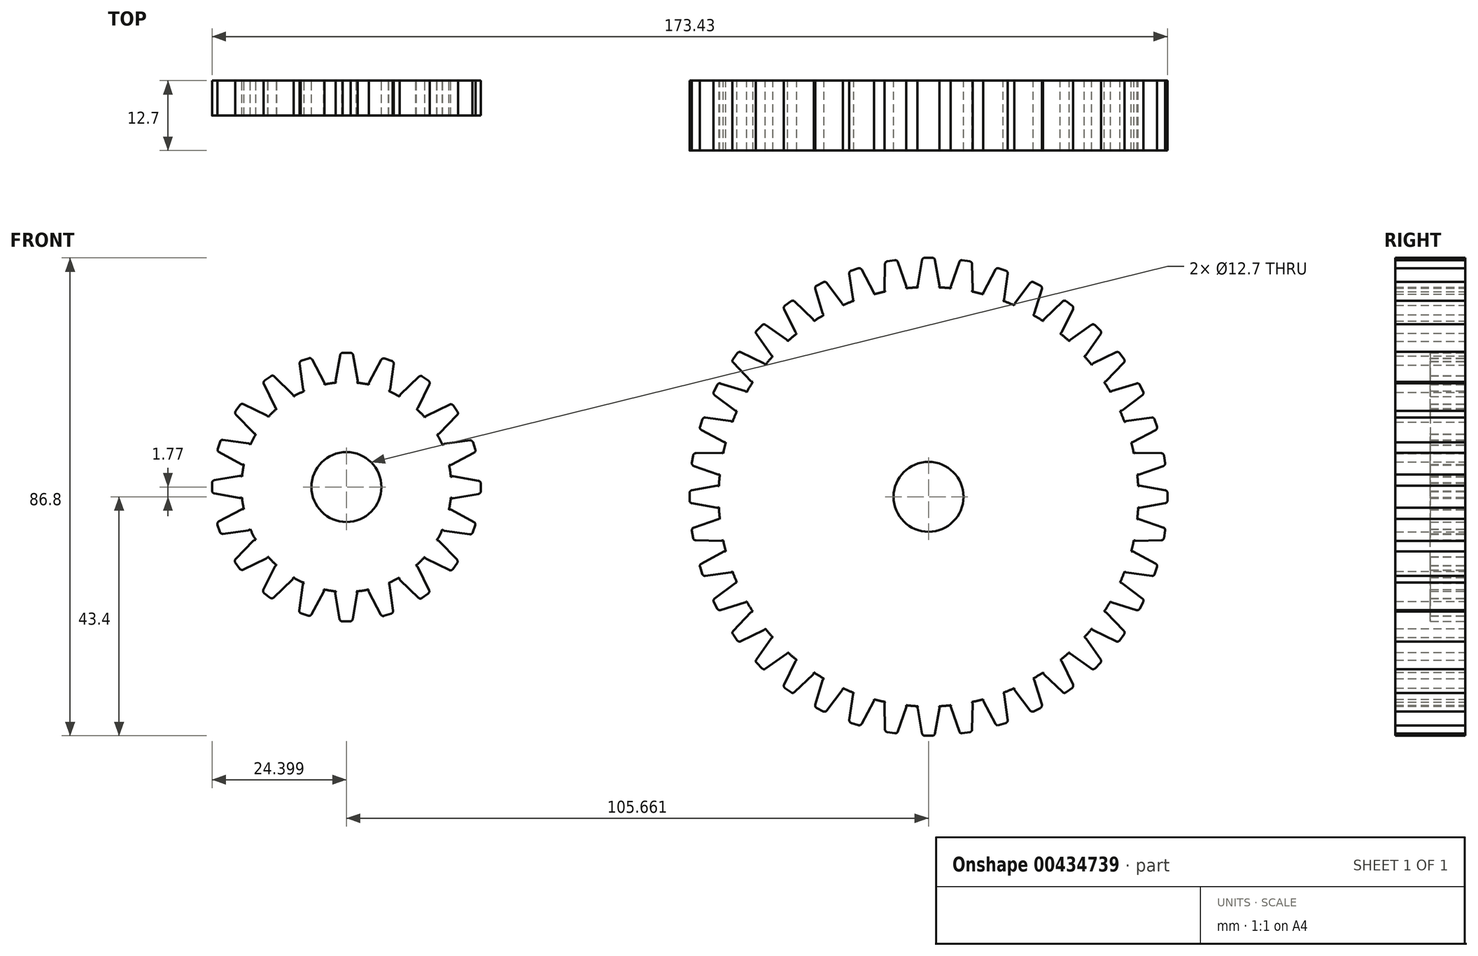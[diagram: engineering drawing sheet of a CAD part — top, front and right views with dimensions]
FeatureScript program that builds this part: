
annotation { "Feature Type Name" : "Feature", "Feature Type Description" : "" }
export const myFeature = defineFeature(function(context is Context, id is Id, definition is map)
    precondition{}
    {
        {
            var Q0;
            Q0=qCreatedBy(makeId("Front.planeOp"),FACE);
            var sketch = newSketch(context, id + "F0", { "sketchPlane" : qUnion([Q0])});
            skCircle(sketch, "E0", {"center": v(0, 0) * mm, "radius": 38.1 * mm});
            skCircle(sketch, "E1", {"center": v(-105.66, 1.77) * mm, "radius": 19.05 * mm});
            skCircle(sketch, "E2", {"center": v(0, 0) * mm, "radius": 6.35 * mm});
            skCircle(sketch, "E3", {"center": v(-105.66, 1.77) * mm, "radius": 6.35 * mm});
            skSolve(sketch);
        }
        {
            var Q0;
            Q0=makeQuery(id+"F0.imprint","IMPRINT",FACE,{"disambiguationData":[TD([[makeQuery(id+"F0.imprint","IMPRINT",EDGE,{"derivedFrom":sQuery(id+"F0.wireOp",EDGE,"E0")}),1.0]])]});
            extrude(context, id + "F1", {"entities" : qUnion([Q0]), "depth" : 12.7 * mm});
        }
        {
            var Q0;
            Q0 = qSketchRegion(id + "F0", true);
            extrude(context, id + "F2", {"entities" : qUnion([Q0]), "operationType" : NewBodyOperationType.ADD, "depth" : 6.35 * mm});
        }
        {
            var Q0;
            Q0=qCreatedBy(makeId("Front.planeOp"),FACE);
            var sketch = newSketch(context, id + "F3", { "sketchPlane" : qUnion([Q0])});
            skLineSegment(sketch, "E4", {"start": v(-1.99, 38.41) * mm, "end": v(-1.18, 42.98) * mm});
            skLineSegment(sketch, "E5", {"start": v(-0.68, 43.4) * mm, "end": v(0.68, 43.4) * mm});
            skLineSegment(sketch, "E6", {"start": v(1.18, 42.98) * mm, "end": v(1.99, 38.41) * mm});
            skLineSegment(sketch, "E7", {"start": v(-1.49, 37.82) * mm, "end": v(1.49, 37.82) * mm});
            skPoint(sketch, "E8.visualSharp", {"position": v(-1.1, 43.4) * mm});
            skArc(sketch, "E8.filletArc", {"start": v(-0.68, 43.4) * mm, "mid": v(-1, 43.29) * mm, "end": v(-1.18, 42.98) * mm});
            skPoint(sketch, "E9.visualSharp", {"position": v(1.1, 43.4) * mm});
            skArc(sketch, "E9.filletArc", {"start": v(1.18, 42.98) * mm, "mid": v(1, 43.29) * mm, "end": v(0.68, 43.4) * mm});
            skPoint(sketch, "E10.visualSharp", {"position": v(-2.1, 37.82) * mm});
            skArc(sketch, "E10.filletArc", {"start": v(-1.99, 38.41) * mm, "mid": v(-1.87, 38) * mm, "end": v(-1.49, 37.82) * mm});
            skPoint(sketch, "E11.visualSharp", {"position": v(2.1, 37.82) * mm});
            skArc(sketch, "E11.filletArc", {"start": v(1.49, 37.82) * mm, "mid": v(1.87, 38) * mm, "end": v(1.99, 38.41) * mm});
            skLineSegment(sketch, "E12", {"start": v(0, 43.4) * mm, "end": v(0, 37.82) * mm});
            skLineSegment(sketch, "E13", {"start": v(4.07, 38.25) * mm, "end": v(5.58, 42.64) * mm});
            skLineSegment(sketch, "E14", {"start": v(6.14, 42.97) * mm, "end": v(7.48, 42.76) * mm});
            skLineSegment(sketch, "E15", {"start": v(7.91, 42.27) * mm, "end": v(8, 37.63) * mm});
            skLineSegment(sketch, "E16", {"start": v(4.47, 37.58) * mm, "end": v(7.4, 37.12) * mm});
            skPoint(sketch, "E17.visualSharp", {"position": v(5.72, 43.04) * mm});
            skArc(sketch, "E17.filletArc", {"start": v(6.14, 42.97) * mm, "mid": v(5.8, 42.9) * mm, "end": v(5.58, 42.64) * mm});
            skPoint(sketch, "E18.visualSharp", {"position": v(7.9, 42.7) * mm});
            skArc(sketch, "E18.filletArc", {"start": v(7.91, 42.27) * mm, "mid": v(7.79, 42.6) * mm, "end": v(7.48, 42.76) * mm});
            skPoint(sketch, "E19.visualSharp", {"position": v(3.87, 37.68) * mm});
            skArc(sketch, "E19.filletArc", {"start": v(4.07, 38.25) * mm, "mid": v(4.11, 37.82) * mm, "end": v(4.47, 37.58) * mm});
            skPoint(sketch, "E20.visualSharp", {"position": v(8, 37.02) * mm});
            skArc(sketch, "E20.filletArc", {"start": v(7.4, 37.12) * mm, "mid": v(7.82, 37.23) * mm, "end": v(8, 37.63) * mm});
            skLineSegment(sketch, "E21", {"start": v(6.81, 42.87) * mm, "end": v(5.94, 37.35) * mm});
            skLineSegment(sketch, "E22.0", {"start": v(4.47, 37.58) * mm, "end": v(5.94, 37.35) * mm, "construction": true});
            skLineSegment(sketch, "E23.0", {"start": v(3.87, 37.68) * mm, "end": v(8, 37.02) * mm, "construction": true});
            skLineSegment(sketch, "E24", {"start": v(9.96, 37.15) * mm, "end": v(12.13, 41.25) * mm});
            skLineSegment(sketch, "E25", {"start": v(12.74, 41.5) * mm, "end": v(14.03, 41.07) * mm});
            skLineSegment(sketch, "E26", {"start": v(14.38, 40.52) * mm, "end": v(13.73, 35.92) * mm});
            skLineSegment(sketch, "E27", {"start": v(10.25, 36.43) * mm, "end": v(13.07, 35.51) * mm});
            skPoint(sketch, "E28.visualSharp", {"position": v(12.34, 41.63) * mm});
            skArc(sketch, "E28.filletArc", {"start": v(12.74, 41.5) * mm, "mid": v(12.4, 41.48) * mm, "end": v(12.13, 41.25) * mm});
            skPoint(sketch, "E29.visualSharp", {"position": v(14.44, 40.94) * mm});
            skArc(sketch, "E29.filletArc", {"start": v(14.38, 40.52) * mm, "mid": v(14.3, 40.86) * mm, "end": v(14.03, 41.07) * mm});
            skPoint(sketch, "E30.visualSharp", {"position": v(9.67, 36.62) * mm});
            skArc(sketch, "E30.filletArc", {"start": v(9.96, 37.15) * mm, "mid": v(9.93, 36.72) * mm, "end": v(10.25, 36.43) * mm});
            skPoint(sketch, "E31.visualSharp", {"position": v(13.65, 35.32) * mm});
            skArc(sketch, "E31.filletArc", {"start": v(13.07, 35.51) * mm, "mid": v(13.5, 35.56) * mm, "end": v(13.73, 35.92) * mm});
            skLineSegment(sketch, "E32", {"start": v(13.39, 41.28) * mm, "end": v(11.66, 35.97) * mm});
            skLineSegment(sketch, "E33", {"start": v(15.66, 35.12) * mm, "end": v(18.46, 38.83) * mm});
            skLineSegment(sketch, "E34", {"start": v(19.1, 38.98) * mm, "end": v(20.3, 38.36) * mm});
            skLineSegment(sketch, "E35", {"start": v(20.56, 37.76) * mm, "end": v(19.2, 33.32) * mm});
            skLineSegment(sketch, "E36", {"start": v(15.84, 34.36) * mm, "end": v(18.49, 33.02) * mm});
            skPoint(sketch, "E37.visualSharp", {"position": v(18.71, 39.17) * mm});
            skArc(sketch, "E37.filletArc", {"start": v(19.1, 38.98) * mm, "mid": v(18.75, 39.02) * mm, "end": v(18.46, 38.83) * mm});
            skPoint(sketch, "E38.visualSharp", {"position": v(20.68, 38.17) * mm});
            skArc(sketch, "E38.filletArc", {"start": v(20.56, 37.76) * mm, "mid": v(20.54, 38.1) * mm, "end": v(20.3, 38.36) * mm});
            skPoint(sketch, "E39.visualSharp", {"position": v(15.3, 34.64) * mm});
            skArc(sketch, "E39.filletArc", {"start": v(15.66, 35.12) * mm, "mid": v(15.57, 34.7) * mm, "end": v(15.84, 34.36) * mm});
            skPoint(sketch, "E40.visualSharp", {"position": v(19.02, 32.74) * mm});
            skArc(sketch, "E40.filletArc", {"start": v(18.49, 33.02) * mm, "mid": v(18.91, 33) * mm, "end": v(19.2, 33.32) * mm});
            skLineSegment(sketch, "E41", {"start": v(19.7, 38.67) * mm, "end": v(17.16, 33.7) * mm});
            skLineSegment(sketch, "E42.0", {"start": v(15.84, 34.36) * mm, "end": v(17.16, 33.7) * mm, "construction": true});
            skLineSegment(sketch, "E43.0", {"start": v(15.3, 34.64) * mm, "end": v(19.02, 32.74) * mm, "construction": true});
            skLineSegment(sketch, "E44.0", {"start": v(10.25, 36.43) * mm, "end": v(11.66, 35.97) * mm, "construction": true});
            skLineSegment(sketch, "E45.0", {"start": v(9.67, 36.62) * mm, "end": v(13.65, 35.32) * mm, "construction": true});
            skLineSegment(sketch, "E46", {"start": v(20.97, 32.26) * mm, "end": v(24.3, 35.48) * mm});
            skLineSegment(sketch, "E47", {"start": v(24.96, 35.53) * mm, "end": v(26.06, 34.73) * mm});
            skLineSegment(sketch, "E48", {"start": v(26.22, 34.1) * mm, "end": v(24.18, 29.92) * mm});
            skLineSegment(sketch, "E49", {"start": v(21.02, 31.48) * mm, "end": v(23.43, 29.73) * mm});
            skPoint(sketch, "E50.visualSharp", {"position": v(24.61, 35.78) * mm});
            skArc(sketch, "E50.filletArc", {"start": v(24.96, 35.53) * mm, "mid": v(24.62, 35.62) * mm, "end": v(24.3, 35.48) * mm});
            skPoint(sketch, "E51.visualSharp", {"position": v(26.4, 34.48) * mm});
            skArc(sketch, "E51.filletArc", {"start": v(26.22, 34.1) * mm, "mid": v(26.25, 34.44) * mm, "end": v(26.06, 34.73) * mm});
            skPoint(sketch, "E52.visualSharp", {"position": v(20.53, 31.84) * mm});
            skArc(sketch, "E52.filletArc", {"start": v(20.97, 32.26) * mm, "mid": v(20.81, 31.85) * mm, "end": v(21.02, 31.48) * mm});
            skPoint(sketch, "E53.visualSharp", {"position": v(23.91, 29.38) * mm});
            skArc(sketch, "E53.filletArc", {"start": v(23.43, 29.73) * mm, "mid": v(23.85, 29.65) * mm, "end": v(24.18, 29.92) * mm});
            skLineSegment(sketch, "E54", {"start": v(25.5, 35.13) * mm, "end": v(22.22, 30.6) * mm});
            skLineSegment(sketch, "E55", {"start": v(25.77, 28.56) * mm, "end": v(29.57, 31.23) * mm});
            skLineSegment(sketch, "E56", {"start": v(30.22, 31.17) * mm, "end": v(31.18, 30.2) * mm});
            skLineSegment(sketch, "E57", {"start": v(31.24, 29.56) * mm, "end": v(28.58, 25.75) * mm});
            skLineSegment(sketch, "E58", {"start": v(25.7, 27.79) * mm, "end": v(27.8, 25.69) * mm});
            skPoint(sketch, "E59.visualSharp", {"position": v(29.92, 31.47) * mm});
            skArc(sketch, "E59.filletArc", {"start": v(30.22, 31.17) * mm, "mid": v(29.9, 31.32) * mm, "end": v(29.57, 31.23) * mm});
            skPoint(sketch, "E60.visualSharp", {"position": v(31.48, 29.9) * mm});
            skArc(sketch, "E60.filletArc", {"start": v(31.24, 29.56) * mm, "mid": v(31.33, 29.9) * mm, "end": v(31.18, 30.2) * mm});
            skPoint(sketch, "E61.visualSharp", {"position": v(25.27, 28.22) * mm});
            skArc(sketch, "E61.filletArc", {"start": v(25.77, 28.56) * mm, "mid": v(25.55, 28.2) * mm, "end": v(25.7, 27.79) * mm});
            skPoint(sketch, "E62.visualSharp", {"position": v(28.23, 25.26) * mm});
            skArc(sketch, "E62.filletArc", {"start": v(27.8, 25.69) * mm, "mid": v(28.2, 25.54) * mm, "end": v(28.58, 25.75) * mm});
            skLineSegment(sketch, "E63", {"start": v(30.7, 30.69) * mm, "end": v(26.75, 26.74) * mm});
            skLineSegment(sketch, "E64.0", {"start": v(25.7, 27.79) * mm, "end": v(26.75, 26.74) * mm, "construction": true});
            skLineSegment(sketch, "E65.0", {"start": v(25.27, 28.22) * mm, "end": v(28.23, 25.26) * mm, "construction": true});
            skLineSegment(sketch, "E66", {"start": v(29.89, 24.22) * mm, "end": v(34.06, 26.25) * mm});
            skLineSegment(sketch, "E67", {"start": v(34.7, 26.1) * mm, "end": v(35.5, 25) * mm});
            skLineSegment(sketch, "E68", {"start": v(35.45, 24.34) * mm, "end": v(32.22, 21) * mm});
            skLineSegment(sketch, "E69", {"start": v(29.7, 23.46) * mm, "end": v(31.44, 21.06) * mm});
            skPoint(sketch, "E70.visualSharp", {"position": v(34.44, 26.44) * mm});
            skArc(sketch, "E70.filletArc", {"start": v(34.7, 26.1) * mm, "mid": v(34.4, 26.29) * mm, "end": v(34.06, 26.25) * mm});
            skPoint(sketch, "E71.visualSharp", {"position": v(35.74, 24.65) * mm});
            skArc(sketch, "E71.filletArc", {"start": v(35.45, 24.34) * mm, "mid": v(35.59, 24.66) * mm, "end": v(35.5, 25) * mm});
            skPoint(sketch, "E72.visualSharp", {"position": v(29.34, 23.95) * mm});
            skArc(sketch, "E72.filletArc", {"start": v(29.89, 24.22) * mm, "mid": v(29.62, 23.88) * mm, "end": v(29.7, 23.46) * mm});
            skPoint(sketch, "E73.visualSharp", {"position": v(31.8, 20.57) * mm});
            skArc(sketch, "E73.filletArc", {"start": v(31.44, 21.06) * mm, "mid": v(31.82, 20.85) * mm, "end": v(32.22, 21) * mm});
            skLineSegment(sketch, "E74", {"start": v(35.1, 25.54) * mm, "end": v(30.57, 22.26) * mm});
            skLineSegment(sketch, "E75", {"start": v(33.31, 19.22) * mm, "end": v(37.75, 20.58) * mm});
            skLineSegment(sketch, "E76", {"start": v(38.35, 20.32) * mm, "end": v(38.97, 19.11) * mm});
            skLineSegment(sketch, "E77", {"start": v(38.82, 18.47) * mm, "end": v(35.11, 15.68) * mm});
            skLineSegment(sketch, "E78", {"start": v(33, 18.5) * mm, "end": v(34.36, 15.86) * mm});
            skPoint(sketch, "E79.visualSharp", {"position": v(38.16, 20.7) * mm});
            skArc(sketch, "E79.filletArc", {"start": v(38.35, 20.32) * mm, "mid": v(38.1, 20.56) * mm, "end": v(37.75, 20.58) * mm});
            skPoint(sketch, "E80.visualSharp", {"position": v(39.16, 18.73) * mm});
            skArc(sketch, "E80.filletArc", {"start": v(38.82, 18.47) * mm, "mid": v(39.01, 18.77) * mm, "end": v(38.97, 19.11) * mm});
            skPoint(sketch, "E81.visualSharp", {"position": v(32.73, 19.04) * mm});
            skArc(sketch, "E81.filletArc", {"start": v(33.31, 19.22) * mm, "mid": v(33, 18.93) * mm, "end": v(33, 18.5) * mm});
            skPoint(sketch, "E82.visualSharp", {"position": v(34.63, 15.32) * mm});
            skArc(sketch, "E82.filletArc", {"start": v(34.36, 15.86) * mm, "mid": v(34.7, 15.6) * mm, "end": v(35.11, 15.68) * mm});
            skLineSegment(sketch, "E83", {"start": v(38.66, 19.72) * mm, "end": v(33.68, 17.18) * mm});
            skLineSegment(sketch, "E84.0", {"start": v(33, 18.5) * mm, "end": v(33.68, 17.18) * mm, "construction": true});
            skLineSegment(sketch, "E85.0", {"start": v(32.73, 19.04) * mm, "end": v(34.63, 15.32) * mm, "construction": true});
            skLineSegment(sketch, "E86.0", {"start": v(29.7, 23.46) * mm, "end": v(30.57, 22.26) * mm, "construction": true});
            skLineSegment(sketch, "E87.0", {"start": v(29.34, 23.95) * mm, "end": v(31.8, 20.57) * mm, "construction": true});
            skLineSegment(sketch, "E88.0", {"start": v(21.02, 31.48) * mm, "end": v(22.22, 30.6) * mm, "construction": true});
            skLineSegment(sketch, "E89.0", {"start": v(20.53, 31.84) * mm, "end": v(23.91, 29.38) * mm, "construction": true});
            skLineSegment(sketch, "E90", {"start": v(35.9, 13.73) * mm, "end": v(40.5, 14.38) * mm});
            skLineSegment(sketch, "E91", {"start": v(41.05, 14.03) * mm, "end": v(41.47, 12.74) * mm});
            skLineSegment(sketch, "E92", {"start": v(41.23, 12.14) * mm, "end": v(37.13, 9.96) * mm});
            skLineSegment(sketch, "E93", {"start": v(35.5, 13.07) * mm, "end": v(36.4, 10.25) * mm});
            skPoint(sketch, "E94.visualSharp", {"position": v(40.92, 14.44) * mm});
            skArc(sketch, "E94.filletArc", {"start": v(41.05, 14.03) * mm, "mid": v(40.84, 14.3) * mm, "end": v(40.5, 14.38) * mm});
            skPoint(sketch, "E95.visualSharp", {"position": v(41.6, 12.34) * mm});
            skArc(sketch, "E95.filletArc", {"start": v(41.23, 12.14) * mm, "mid": v(41.46, 12.4) * mm, "end": v(41.47, 12.74) * mm});
            skPoint(sketch, "E96.visualSharp", {"position": v(35.3, 13.65) * mm});
            skArc(sketch, "E96.filletArc", {"start": v(35.9, 13.73) * mm, "mid": v(35.54, 13.5) * mm, "end": v(35.5, 13.07) * mm});
            skPoint(sketch, "E97.visualSharp", {"position": v(36.6, 9.67) * mm});
            skArc(sketch, "E97.filletArc", {"start": v(36.4, 10.25) * mm, "mid": v(36.7, 9.93) * mm, "end": v(37.13, 9.96) * mm});
            skLineSegment(sketch, "E98", {"start": v(41.26, 13.39) * mm, "end": v(35.95, 11.66) * mm});
            skLineSegment(sketch, "E99.0", {"start": v(35.5, 13.07) * mm, "end": v(35.95, 11.66) * mm, "construction": true});
            skLineSegment(sketch, "E100", {"start": v(37.6, 8) * mm, "end": v(42.24, 7.9) * mm});
            skLineSegment(sketch, "E101", {"start": v(42.73, 7.48) * mm, "end": v(42.95, 6.14) * mm});
            skLineSegment(sketch, "E102", {"start": v(42.6, 5.58) * mm, "end": v(38.22, 4.07) * mm});
            skLineSegment(sketch, "E103", {"start": v(37.09, 7.4) * mm, "end": v(37.55, 4.47) * mm});
            skPoint(sketch, "E104.visualSharp", {"position": v(42.67, 7.9) * mm});
            skArc(sketch, "E104.filletArc", {"start": v(42.73, 7.48) * mm, "mid": v(42.56, 7.79) * mm, "end": v(42.24, 7.9) * mm});
            skPoint(sketch, "E105.visualSharp", {"position": v(43.01, 5.72) * mm});
            skArc(sketch, "E105.filletArc", {"start": v(42.6, 5.58) * mm, "mid": v(42.88, 5.8) * mm, "end": v(42.95, 6.14) * mm});
            skPoint(sketch, "E106.visualSharp", {"position": v(37, 8) * mm});
            skArc(sketch, "E106.filletArc", {"start": v(37.6, 8) * mm, "mid": v(37.2, 7.82) * mm, "end": v(37.09, 7.4) * mm});
            skPoint(sketch, "E107.visualSharp", {"position": v(37.65, 3.87) * mm});
            skArc(sketch, "E107.filletArc", {"start": v(37.55, 4.47) * mm, "mid": v(37.8, 4.11) * mm, "end": v(38.22, 4.07) * mm});
            skLineSegment(sketch, "E108", {"start": v(42.84, 6.81) * mm, "end": v(37.32, 5.94) * mm});
            skLineSegment(sketch, "E109", {"start": v(38.38, 1.99) * mm, "end": v(42.95, 1.18) * mm});
            skLineSegment(sketch, "E110", {"start": v(43.37, 0.68) * mm, "end": v(43.37, -0.68) * mm});
            skLineSegment(sketch, "E111", {"start": v(42.95, -1.18) * mm, "end": v(38.38, -1.99) * mm});
            skLineSegment(sketch, "E112", {"start": v(37.79, 1.48) * mm, "end": v(37.79, -1.49) * mm});
            skPoint(sketch, "E113.visualSharp", {"position": v(43.37, 1.1) * mm});
            skArc(sketch, "E113.filletArc", {"start": v(43.37, 0.68) * mm, "mid": v(43.25, 1) * mm, "end": v(42.95, 1.18) * mm});
            skPoint(sketch, "E114.visualSharp", {"position": v(43.37, -1.1) * mm});
            skArc(sketch, "E114.filletArc", {"start": v(42.95, -1.18) * mm, "mid": v(43.25, -1) * mm, "end": v(43.37, -0.68) * mm});
            skPoint(sketch, "E115.visualSharp", {"position": v(37.79, 2.1) * mm});
            skArc(sketch, "E115.filletArc", {"start": v(38.38, 1.99) * mm, "mid": v(37.97, 1.87) * mm, "end": v(37.79, 1.48) * mm});
            skPoint(sketch, "E116.visualSharp", {"position": v(37.79, -2.1) * mm});
            skArc(sketch, "E116.filletArc", {"start": v(37.79, -1.49) * mm, "mid": v(37.97, -1.88) * mm, "end": v(38.38, -1.99) * mm});
            skLineSegment(sketch, "E117", {"start": v(43.37, 0) * mm, "end": v(37.79, 0) * mm});
            skLineSegment(sketch, "E118.0", {"start": v(37.79, 1.48) * mm, "end": v(37.79, 0) * mm, "construction": true});
            skLineSegment(sketch, "E119.0", {"start": v(37.79, 2.1) * mm, "end": v(37.79, -2.1) * mm, "construction": true});
            skLineSegment(sketch, "E120.0", {"start": v(37.09, 7.4) * mm, "end": v(37.32, 5.94) * mm, "construction": true});
            skLineSegment(sketch, "E121.0", {"start": v(37, 8) * mm, "end": v(37.65, 3.87) * mm, "construction": true});
            skArc(sketch, "E122.MirrorCS", {"start": v(-4.07, 38.25) * mm, "mid": v(-4.11, 37.82) * mm, "end": v(-4.47, 37.58) * mm});
            skArc(sketch, "E123.MirrorCS", {"start": v(-37.6, 8) * mm, "mid": v(-37.2, 7.82) * mm, "end": v(-37.09, 7.4) * mm});
            skLineSegment(sketch, "E124.MirrorCS", {"start": v(-37.09, 7.4) * mm, "end": v(-37.32, 5.94) * mm, "construction": true});
            skLineSegment(sketch, "E125.MirrorCS", {"start": v(-4.47, 37.58) * mm, "end": v(-5.94, 37.35) * mm, "construction": true});
            skLineSegment(sketch, "E126.MirrorCS", {"start": v(-4.47, 37.58) * mm, "end": v(-7.4, 37.12) * mm});
            skArc(sketch, "E127.MirrorCS", {"start": v(-27.8, 25.69) * mm, "mid": v(-28.2, 25.54) * mm, "end": v(-28.58, 25.75) * mm});
            skLineSegment(sketch, "E128.MirrorCS", {"start": v(-33, 18.5) * mm, "end": v(-34.36, 15.86) * mm});
            skArc(sketch, "E129.MirrorCS", {"start": v(-25.77, 28.56) * mm, "mid": v(-25.55, 28.2) * mm, "end": v(-25.7, 27.79) * mm});
            skArc(sketch, "E130.MirrorCS", {"start": v(-9.96, 37.15) * mm, "mid": v(-9.93, 36.72) * mm, "end": v(-10.25, 36.43) * mm});
            skLineSegment(sketch, "E131.MirrorCS", {"start": v(-35.5, 13.07) * mm, "end": v(-35.95, 11.66) * mm, "construction": true});
            skArc(sketch, "E132.MirrorCS", {"start": v(-38.38, 1.99) * mm, "mid": v(-37.97, 1.87) * mm, "end": v(-37.79, 1.48) * mm});
            skLineSegment(sketch, "E133.MirrorCS", {"start": v(-10.25, 36.43) * mm, "end": v(-11.66, 35.97) * mm, "construction": true});
            skLineSegment(sketch, "E134.MirrorCS", {"start": v(-25.7, 27.79) * mm, "end": v(-27.8, 25.69) * mm});
            skArc(sketch, "E135.MirrorCS", {"start": v(-29.89, 24.22) * mm, "mid": v(-29.62, 23.88) * mm, "end": v(-29.7, 23.46) * mm});
            skLineSegment(sketch, "E136.MirrorCS", {"start": v(-21.02, 31.48) * mm, "end": v(-22.22, 30.6) * mm, "construction": true});
            skLineSegment(sketch, "E137.MirrorCS", {"start": v(-37.09, 7.4) * mm, "end": v(-37.55, 4.47) * mm});
            skLineSegment(sketch, "E138.MirrorCS", {"start": v(-3.87, 37.68) * mm, "end": v(-8, 37.02) * mm, "construction": true});
            skLineSegment(sketch, "E139.MirrorCS", {"start": v(-29.7, 23.46) * mm, "end": v(-30.57, 22.26) * mm, "construction": true});
            skLineSegment(sketch, "E140.MirrorCS", {"start": v(-37.79, 1.48) * mm, "end": v(-37.79, 0) * mm, "construction": true});
            skLineSegment(sketch, "E141.MirrorCS", {"start": v(-21.02, 31.48) * mm, "end": v(-23.43, 29.73) * mm});
            skLineSegment(sketch, "E142.MirrorCS", {"start": v(-25.27, 28.22) * mm, "end": v(-28.23, 25.26) * mm, "construction": true});
            skArc(sketch, "E143.MirrorCS", {"start": v(-33.31, 19.22) * mm, "mid": v(-33, 18.93) * mm, "end": v(-33, 18.5) * mm});
            skArc(sketch, "E144.MirrorCS", {"start": v(-7.4, 37.12) * mm, "mid": v(-7.82, 37.23) * mm, "end": v(-8, 37.63) * mm});
            skLineSegment(sketch, "E145.MirrorCS", {"start": v(-33, 18.5) * mm, "end": v(-33.68, 17.18) * mm, "construction": true});
            skArc(sketch, "E146.MirrorCS", {"start": v(-35.9, 13.73) * mm, "mid": v(-35.54, 13.5) * mm, "end": v(-35.5, 13.07) * mm});
            skArc(sketch, "E147.MirrorCS", {"start": v(-20.97, 32.26) * mm, "mid": v(-20.81, 31.85) * mm, "end": v(-21.02, 31.48) * mm});
            skLineSegment(sketch, "E148.MirrorCS", {"start": v(-25.7, 27.79) * mm, "end": v(-26.75, 26.74) * mm, "construction": true});
            skLineSegment(sketch, "E149.MirrorCS", {"start": v(-15.84, 34.36) * mm, "end": v(-18.49, 33.02) * mm});
            skLineSegment(sketch, "E150.MirrorCS", {"start": v(-35.5, 13.07) * mm, "end": v(-36.4, 10.25) * mm});
            skLineSegment(sketch, "E151.MirrorCS", {"start": v(-9.67, 36.62) * mm, "end": v(-13.65, 35.32) * mm, "construction": true});
            skArc(sketch, "E152.MirrorCS", {"start": v(-37.55, 4.47) * mm, "mid": v(-37.8, 4.11) * mm, "end": v(-38.22, 4.07) * mm});
            skLineSegment(sketch, "E153.MirrorCS", {"start": v(-10.25, 36.43) * mm, "end": v(-13.07, 35.51) * mm});
            skLineSegment(sketch, "E154.MirrorCS", {"start": v(-15.3, 34.64) * mm, "end": v(-19.02, 32.74) * mm, "construction": true});
            skArc(sketch, "E155.MirrorCS", {"start": v(-1.49, 37.82) * mm, "mid": v(-1.87, 38) * mm, "end": v(-1.99, 38.41) * mm});
            skLineSegment(sketch, "E156.MirrorCS", {"start": v(1.49, 37.82) * mm, "end": v(-1.49, 37.82) * mm});
            skArc(sketch, "E157.MirrorCS", {"start": v(-26.22, 34.1) * mm, "mid": v(-26.25, 34.44) * mm, "end": v(-26.06, 34.73) * mm});
            skLineSegment(sketch, "E158.MirrorCS", {"start": v(-38.35, 20.32) * mm, "end": v(-38.97, 19.11) * mm});
            skLineSegment(sketch, "E159.MirrorCS", {"start": v(-15.84, 34.36) * mm, "end": v(-17.16, 33.7) * mm, "construction": true});
            skArc(sketch, "E160.MirrorCS", {"start": v(-31.44, 21.06) * mm, "mid": v(-31.82, 20.85) * mm, "end": v(-32.22, 21) * mm});
            skLineSegment(sketch, "E161.MirrorCS", {"start": v(-20.53, 31.84) * mm, "end": v(-23.91, 29.38) * mm, "construction": true});
            skLineSegment(sketch, "E162.MirrorCS", {"start": v(-37, 8) * mm, "end": v(-37.65, 3.87) * mm, "construction": true});
            skArc(sketch, "E163.MirrorCS", {"start": v(-18.49, 33.02) * mm, "mid": v(-18.91, 33) * mm, "end": v(-19.2, 33.32) * mm});
            skLineSegment(sketch, "E164.MirrorCS", {"start": v(-19.1, 38.98) * mm, "end": v(-20.3, 38.36) * mm});
            skArc(sketch, "E165.MirrorCS", {"start": v(-24.96, 35.53) * mm, "mid": v(-24.62, 35.62) * mm, "end": v(-24.3, 35.48) * mm});
            skArc(sketch, "E166.MirrorCS", {"start": v(-34.36, 15.86) * mm, "mid": v(-34.7, 15.6) * mm, "end": v(-35.11, 15.68) * mm});
            skLineSegment(sketch, "E167.MirrorCS", {"start": v(-24.96, 35.53) * mm, "end": v(-26.06, 34.73) * mm});
            skArc(sketch, "E168.MirrorCS", {"start": v(-13.07, 35.51) * mm, "mid": v(-13.5, 35.56) * mm, "end": v(-13.73, 35.92) * mm});
            skArc(sketch, "E169.MirrorCS", {"start": v(-15.66, 35.12) * mm, "mid": v(-15.57, 34.7) * mm, "end": v(-15.84, 34.36) * mm});
            skArc(sketch, "E170.MirrorCS", {"start": v(-20.56, 37.76) * mm, "mid": v(-20.54, 38.1) * mm, "end": v(-20.3, 38.36) * mm});
            skArc(sketch, "E171.MirrorCS", {"start": v(-23.43, 29.73) * mm, "mid": v(-23.85, 29.65) * mm, "end": v(-24.18, 29.92) * mm});
            skLineSegment(sketch, "E172.MirrorCS", {"start": v(-32.73, 19.04) * mm, "end": v(-34.63, 15.32) * mm, "construction": true});
            skArc(sketch, "E173.MirrorCS", {"start": v(-19.1, 38.98) * mm, "mid": v(-18.75, 39.02) * mm, "end": v(-18.46, 38.83) * mm});
            skArc(sketch, "E174.MirrorCS", {"start": v(-38.82, 18.47) * mm, "mid": v(-39.01, 18.77) * mm, "end": v(-38.97, 19.11) * mm});
            skArc(sketch, "E175.MirrorCS", {"start": v(-41.23, 12.14) * mm, "mid": v(-41.46, 12.4) * mm, "end": v(-41.47, 12.74) * mm});
            skLineSegment(sketch, "E176.MirrorCS", {"start": v(-37.79, 1.48) * mm, "end": v(-37.79, -1.49) * mm});
            skLineSegment(sketch, "E177.MirrorCS", {"start": v(-29.7, 23.46) * mm, "end": v(-31.44, 21.06) * mm});
            skArc(sketch, "E178.MirrorCS", {"start": v(-36.4, 10.25) * mm, "mid": v(-36.7, 9.93) * mm, "end": v(-37.13, 9.96) * mm});
            skArc(sketch, "E179.MirrorCS", {"start": v(-14.38, 40.52) * mm, "mid": v(-14.3, 40.86) * mm, "end": v(-14.03, 41.07) * mm});
            skLineSegment(sketch, "E180.MirrorCS", {"start": v(-41.05, 14.03) * mm, "end": v(-41.47, 12.74) * mm});
            skArc(sketch, "E181.MirrorCS", {"start": v(-30.22, 31.17) * mm, "mid": v(-29.9, 31.32) * mm, "end": v(-29.57, 31.23) * mm});
            skArc(sketch, "E182.MirrorCS", {"start": v(1.99, 38.41) * mm, "mid": v(1.87, 38) * mm, "end": v(1.49, 37.82) * mm});
            skArc(sketch, "E183.MirrorCS", {"start": v(-1.18, 42.98) * mm, "mid": v(-1, 43.29) * mm, "end": v(-0.68, 43.4) * mm});
            skArc(sketch, "E184.MirrorCS", {"start": v(0.68, 43.4) * mm, "mid": v(1, 43.29) * mm, "end": v(1.18, 42.98) * mm});
            skLineSegment(sketch, "E185.MirrorCS", {"start": v(0.68, 43.4) * mm, "end": v(-0.68, 43.4) * mm});
            skArc(sketch, "E186.MirrorCS", {"start": v(-41.05, 14.03) * mm, "mid": v(-40.84, 14.3) * mm, "end": v(-40.5, 14.38) * mm});
            skArc(sketch, "E187.MirrorCS", {"start": v(-38.35, 20.32) * mm, "mid": v(-38.1, 20.56) * mm, "end": v(-37.75, 20.58) * mm});
            skLineSegment(sketch, "E188.MirrorCS", {"start": v(-6.14, 42.97) * mm, "end": v(-7.48, 42.76) * mm});
            skLineSegment(sketch, "E189.MirrorCS", {"start": v(-41.23, 12.14) * mm, "end": v(-37.13, 9.96) * mm});
            skLineSegment(sketch, "E190.MirrorCS", {"start": v(-34.7, 26.1) * mm, "end": v(-35.5, 25) * mm});
            skArc(sketch, "E191.MirrorCS", {"start": v(-12.74, 41.5) * mm, "mid": v(-12.4, 41.48) * mm, "end": v(-12.13, 41.25) * mm});
            skArc(sketch, "E192.MirrorCS", {"start": v(-31.24, 29.56) * mm, "mid": v(-31.33, 29.9) * mm, "end": v(-31.18, 30.2) * mm});
            skArc(sketch, "E193.MirrorCS", {"start": v(-42.6, 5.58) * mm, "mid": v(-42.88, 5.8) * mm, "end": v(-42.95, 6.14) * mm});
            skLineSegment(sketch, "E194.MirrorCS", {"start": v(-12.74, 41.5) * mm, "end": v(-14.03, 41.07) * mm});
            skArc(sketch, "E195.MirrorCS", {"start": v(-42.73, 7.48) * mm, "mid": v(-42.56, 7.79) * mm, "end": v(-42.24, 7.9) * mm});
            skLineSegment(sketch, "E196.MirrorCS", {"start": v(-30.22, 31.17) * mm, "end": v(-31.18, 30.2) * mm});
            skArc(sketch, "E197.MirrorCS", {"start": v(-35.45, 24.34) * mm, "mid": v(-35.59, 24.66) * mm, "end": v(-35.5, 25) * mm});
            skLineSegment(sketch, "E198.MirrorCS", {"start": v(-29.34, 23.95) * mm, "end": v(-31.8, 20.57) * mm, "construction": true});
            skArc(sketch, "E199.MirrorCS", {"start": v(-7.91, 42.27) * mm, "mid": v(-7.79, 42.6) * mm, "end": v(-7.48, 42.76) * mm});
            skLineSegment(sketch, "E200.MirrorCS", {"start": v(-37.79, 2.1) * mm, "end": v(-37.79, -2.1) * mm, "construction": true});
            skArc(sketch, "E201.MirrorCS", {"start": v(-34.7, 26.1) * mm, "mid": v(-34.4, 26.29) * mm, "end": v(-34.06, 26.25) * mm});
            skArc(sketch, "E202.MirrorCS", {"start": v(-6.14, 42.97) * mm, "mid": v(-5.8, 42.9) * mm, "end": v(-5.58, 42.64) * mm});
            skArc(sketch, "E203.MirrorCS", {"start": v(-37.79, -1.49) * mm, "mid": v(-37.97, -1.88) * mm, "end": v(-38.38, -1.99) * mm});
            skLineSegment(sketch, "E204.MirrorCS", {"start": v(-42.73, 7.48) * mm, "end": v(-42.95, 6.14) * mm});
            skLineSegment(sketch, "E205.MirrorCS", {"start": v(-35.45, 24.34) * mm, "end": v(-32.22, 21) * mm});
            skLineSegment(sketch, "E206.MirrorCS", {"start": v(-20.97, 32.26) * mm, "end": v(-24.3, 35.48) * mm});
            skLineSegment(sketch, "E207.MirrorCS", {"start": v(-43.37, 0.68) * mm, "end": v(-43.37, -0.68) * mm});
            skArc(sketch, "E208.MirrorCS", {"start": v(-42.95, -1.18) * mm, "mid": v(-43.25, -1) * mm, "end": v(-43.37, -0.68) * mm});
            skLineSegment(sketch, "E209.MirrorCS", {"start": v(-9.96, 37.15) * mm, "end": v(-12.13, 41.25) * mm});
            skLineSegment(sketch, "E210.MirrorCS", {"start": v(-25.77, 28.56) * mm, "end": v(-29.57, 31.23) * mm});
            skLineSegment(sketch, "E211.MirrorCS", {"start": v(-15.66, 35.12) * mm, "end": v(-18.46, 38.83) * mm});
            skArc(sketch, "E212.MirrorCS", {"start": v(-43.37, 0.68) * mm, "mid": v(-43.25, 1) * mm, "end": v(-42.95, 1.18) * mm});
            skLineSegment(sketch, "E213.MirrorCS", {"start": v(-38.82, 18.47) * mm, "end": v(-35.11, 15.68) * mm});
            skLineSegment(sketch, "E214.MirrorCS", {"start": v(-4.07, 38.25) * mm, "end": v(-5.58, 42.64) * mm});
            skLineSegment(sketch, "E215.MirrorCS", {"start": v(-20.56, 37.76) * mm, "end": v(-19.2, 33.32) * mm});
            skLineSegment(sketch, "E216.MirrorCS", {"start": v(-19.7, 38.67) * mm, "end": v(-17.16, 33.7) * mm});
            skLineSegment(sketch, "E217.MirrorCS", {"start": v(-31.24, 29.56) * mm, "end": v(-28.58, 25.75) * mm});
            skLineSegment(sketch, "E218.MirrorCS", {"start": v(-42.6, 5.58) * mm, "end": v(-38.22, 4.07) * mm});
            skLineSegment(sketch, "E219.MirrorCS", {"start": v(-26.22, 34.1) * mm, "end": v(-24.18, 29.92) * mm});
            skPoint(sketch, "E220.MirrorP", {"position": v(-13.65, 35.32) * mm});
            skLineSegment(sketch, "E221.MirrorCS", {"start": v(-38.38, 1.99) * mm, "end": v(-42.95, 1.18) * mm});
            skLineSegment(sketch, "E222.MirrorCS", {"start": v(-33.31, 19.22) * mm, "end": v(-37.75, 20.58) * mm});
            skPoint(sketch, "E223.MirrorP", {"position": v(-31.8, 20.57) * mm});
            skPoint(sketch, "E224.MirrorP", {"position": v(-36.6, 9.67) * mm});
            skLineSegment(sketch, "E225.MirrorCS", {"start": v(-1.18, 42.98) * mm, "end": v(-1.99, 38.41) * mm});
            skLineSegment(sketch, "E226.MirrorCS", {"start": v(1.99, 38.41) * mm, "end": v(1.18, 42.98) * mm});
            skLineSegment(sketch, "E227.MirrorCS", {"start": v(-7.91, 42.27) * mm, "end": v(-8, 37.63) * mm});
            skLineSegment(sketch, "E228.MirrorCS", {"start": v(-42.84, 6.81) * mm, "end": v(-37.32, 5.94) * mm});
            skLineSegment(sketch, "E229.MirrorCS", {"start": v(-38.66, 19.72) * mm, "end": v(-33.68, 17.18) * mm});
            skPoint(sketch, "E230.MirrorP", {"position": v(-37.65, 3.87) * mm});
            skPoint(sketch, "E231.MirrorP", {"position": v(-8, 37.02) * mm});
            skPoint(sketch, "E232.MirrorP", {"position": v(-28.23, 25.26) * mm});
            skPoint(sketch, "E233.MirrorP", {"position": v(-34.63, 15.32) * mm});
            skLineSegment(sketch, "E234.MirrorCS", {"start": v(-35.1, 25.54) * mm, "end": v(-30.57, 22.26) * mm});
            skLineSegment(sketch, "E235.MirrorCS", {"start": v(-35.9, 13.73) * mm, "end": v(-40.5, 14.38) * mm});
            skLineSegment(sketch, "E236.MirrorCS", {"start": v(-14.38, 40.52) * mm, "end": v(-13.73, 35.92) * mm});
            skPoint(sketch, "E237.MirrorP", {"position": v(-35.3, 13.65) * mm});
            skPoint(sketch, "E238.MirrorP", {"position": v(-37.79, 2.1) * mm});
            skLineSegment(sketch, "E239.MirrorCS", {"start": v(-41.26, 13.39) * mm, "end": v(-35.95, 11.66) * mm});
            skLineSegment(sketch, "E240.MirrorCS", {"start": v(-29.89, 24.22) * mm, "end": v(-34.06, 26.25) * mm});
            skLineSegment(sketch, "E241.MirrorCS", {"start": v(-30.7, 30.69) * mm, "end": v(-26.75, 26.74) * mm});
            skPoint(sketch, "E242.MirrorP", {"position": v(-35.74, 24.65) * mm});
            skPoint(sketch, "E243.MirrorP", {"position": v(-41.6, 12.34) * mm});
            skPoint(sketch, "E244.MirrorP", {"position": v(-14.44, 40.94) * mm});
            skPoint(sketch, "E245.MirrorP", {"position": v(-26.4, 34.48) * mm});
            skLineSegment(sketch, "E246.MirrorCS", {"start": v(-25.5, 35.13) * mm, "end": v(-22.22, 30.6) * mm});
            skLineSegment(sketch, "E247.MirrorCS", {"start": v(-6.81, 42.87) * mm, "end": v(-5.94, 37.35) * mm});
            skPoint(sketch, "E248.MirrorP", {"position": v(-37, 8) * mm});
            skLineSegment(sketch, "E249.MirrorCS", {"start": v(-37.6, 8) * mm, "end": v(-42.24, 7.9) * mm});
            skPoint(sketch, "E250.MirrorP", {"position": v(-3.87, 37.68) * mm});
            skLineSegment(sketch, "E251.MirrorCS", {"start": v(-13.39, 41.28) * mm, "end": v(-11.66, 35.97) * mm});
            skLineSegment(sketch, "E252.MirrorCS", {"start": v(-43.37, 0) * mm, "end": v(-37.79, 0) * mm});
            skLineSegment(sketch, "E253.MirrorCS", {"start": v(-42.95, -1.18) * mm, "end": v(-38.38, -1.99) * mm});
            skPoint(sketch, "E254.MirrorP", {"position": v(-32.73, 19.04) * mm});
            skPoint(sketch, "E255.MirrorP", {"position": v(-39.16, 18.73) * mm});
            skPoint(sketch, "E256.MirrorP", {"position": v(-20.68, 38.17) * mm});
            skPoint(sketch, "E257.MirrorP", {"position": v(-31.48, 29.9) * mm});
            skPoint(sketch, "E258.MirrorP", {"position": v(-43.01, 5.72) * mm});
            skPoint(sketch, "E259.MirrorP", {"position": v(-23.91, 29.38) * mm});
            skPoint(sketch, "E260.MirrorP", {"position": v(-42.67, 7.9) * mm});
            skPoint(sketch, "E261.MirrorP", {"position": v(-5.72, 43.04) * mm});
            skPoint(sketch, "E262.MirrorP", {"position": v(-18.71, 39.17) * mm});
            skPoint(sketch, "E263.MirrorP", {"position": v(-29.92, 31.47) * mm});
            skPoint(sketch, "E264.MirrorP", {"position": v(-38.16, 20.7) * mm});
            skPoint(sketch, "E265.MirrorP", {"position": v(-37.79, -2.1) * mm});
            skPoint(sketch, "E266.MirrorP", {"position": v(-19.02, 32.74) * mm});
            skPoint(sketch, "E267.MirrorP", {"position": v(-29.34, 23.95) * mm});
            skPoint(sketch, "E268.MirrorP", {"position": v(-9.67, 36.62) * mm});
            skPoint(sketch, "E269.MirrorP", {"position": v(-20.53, 31.84) * mm});
            skPoint(sketch, "E270.MirrorP", {"position": v(-43.37, -1.1) * mm});
            skPoint(sketch, "E271.MirrorP", {"position": v(-43.37, 1.1) * mm});
            skPoint(sketch, "E272.MirrorP", {"position": v(-12.34, 41.63) * mm});
            skPoint(sketch, "E273.MirrorP", {"position": v(-24.61, 35.78) * mm});
            skPoint(sketch, "E274.MirrorP", {"position": v(-15.3, 34.64) * mm});
            skPoint(sketch, "E275.MirrorP", {"position": v(-25.27, 28.22) * mm});
            skPoint(sketch, "E276.MirrorP", {"position": v(-40.92, 14.44) * mm});
            skPoint(sketch, "E277.MirrorP", {"position": v(-34.44, 26.44) * mm});
            skPoint(sketch, "E278.MirrorP", {"position": v(-7.9, 42.7) * mm});
            skLineSegment(sketch, "E279.MirrorCS", {"start": v(1.49, -37.82) * mm, "end": v(-1.49, -37.82) * mm});
            skArc(sketch, "E280.MirrorCS", {"start": v(1.99, -38.41) * mm, "mid": v(1.87, -38) * mm, "end": v(1.49, -37.82) * mm});
            skArc(sketch, "E281.MirrorCS", {"start": v(1.49, -37.82) * mm, "mid": v(1.87, -38) * mm, "end": v(1.99, -38.41) * mm});
            skLineSegment(sketch, "E282.MirrorCS", {"start": v(-1.49, -37.82) * mm, "end": v(1.49, -37.82) * mm});
            skArc(sketch, "E283.MirrorCS", {"start": v(-1.49, -37.82) * mm, "mid": v(-1.87, -38) * mm, "end": v(-1.99, -38.41) * mm});
            skArc(sketch, "E284.MirrorCS", {"start": v(-1.99, -38.41) * mm, "mid": v(-1.87, -38) * mm, "end": v(-1.49, -37.82) * mm});
            skLineSegment(sketch, "E285.MirrorCS", {"start": v(0.68, -43.4) * mm, "end": v(-0.68, -43.4) * mm});
            skArc(sketch, "E286.MirrorCS", {"start": v(0.68, -43.4) * mm, "mid": v(1, -43.29) * mm, "end": v(1.18, -42.98) * mm});
            skArc(sketch, "E287.MirrorCS", {"start": v(-1.18, -42.98) * mm, "mid": v(-1, -43.29) * mm, "end": v(-0.68, -43.4) * mm});
            skArc(sketch, "E288.MirrorCS", {"start": v(4.07, -38.25) * mm, "mid": v(4.11, -37.82) * mm, "end": v(4.47, -37.58) * mm});
            skArc(sketch, "E289.MirrorCS", {"start": v(1.18, -42.98) * mm, "mid": v(1, -43.29) * mm, "end": v(0.68, -43.4) * mm});
            skArc(sketch, "E290.MirrorCS", {"start": v(-0.68, -43.4) * mm, "mid": v(-1, -43.29) * mm, "end": v(-1.18, -42.98) * mm});
            skLineSegment(sketch, "E291.MirrorCS", {"start": v(-0.68, -43.4) * mm, "end": v(0.68, -43.4) * mm});
            skLineSegment(sketch, "E292.MirrorCS", {"start": v(-37.09, -7.4) * mm, "end": v(-37.32, -5.94) * mm, "construction": true});
            skArc(sketch, "E293.MirrorCS", {"start": v(-37.6, -8) * mm, "mid": v(-37.2, -7.82) * mm, "end": v(-37.09, -7.4) * mm});
            skLineSegment(sketch, "E294.MirrorCS", {"start": v(37.09, -7.4) * mm, "end": v(37.55, -4.47) * mm});
            skLineSegment(sketch, "E295.MirrorCS", {"start": v(33, -18.5) * mm, "end": v(34.36, -15.86) * mm});
            skLineSegment(sketch, "E296.MirrorCS", {"start": v(33, -18.5) * mm, "end": v(33.68, -17.18) * mm, "construction": true});
            skArc(sketch, "E297.MirrorCS", {"start": v(35.9, -13.73) * mm, "mid": v(35.54, -13.5) * mm, "end": v(35.5, -13.07) * mm});
            skArc(sketch, "E298.MirrorCS", {"start": v(33.31, -19.22) * mm, "mid": v(33, -18.93) * mm, "end": v(33, -18.5) * mm});
            skLineSegment(sketch, "E299.MirrorCS", {"start": v(35.5, -13.07) * mm, "end": v(35.95, -11.66) * mm, "construction": true});
            skArc(sketch, "E300.MirrorCS", {"start": v(38.38, -1.99) * mm, "mid": v(37.97, -1.87) * mm, "end": v(37.79, -1.48) * mm});
            skLineSegment(sketch, "E301.MirrorCS", {"start": v(4.47, -37.58) * mm, "end": v(5.94, -37.35) * mm, "construction": true});
            skLineSegment(sketch, "E302.MirrorCS", {"start": v(-4.47, -37.58) * mm, "end": v(-5.94, -37.35) * mm, "construction": true});
            skArc(sketch, "E303.MirrorCS", {"start": v(25.77, -28.56) * mm, "mid": v(25.55, -28.2) * mm, "end": v(25.7, -27.79) * mm});
            skLineSegment(sketch, "E304.MirrorCS", {"start": v(10.25, -36.43) * mm, "end": v(11.66, -35.97) * mm, "construction": true});
            skLineSegment(sketch, "E305.MirrorCS", {"start": v(-29.7, -23.46) * mm, "end": v(-30.57, -22.26) * mm, "construction": true});
            skArc(sketch, "E306.MirrorCS", {"start": v(37.55, -4.47) * mm, "mid": v(37.8, -4.11) * mm, "end": v(38.22, -4.07) * mm});
            skArc(sketch, "E307.MirrorCS", {"start": v(37.6, -8) * mm, "mid": v(37.2, -7.82) * mm, "end": v(37.09, -7.4) * mm});
            skArc(sketch, "E308.MirrorCS", {"start": v(-4.07, -38.25) * mm, "mid": v(-4.11, -37.82) * mm, "end": v(-4.47, -37.58) * mm});
            skLineSegment(sketch, "E309.MirrorCS", {"start": v(37, -8) * mm, "end": v(37.65, -3.87) * mm, "construction": true});
            skLineSegment(sketch, "E310.MirrorCS", {"start": v(-21.02, -31.48) * mm, "end": v(-22.22, -30.6) * mm, "construction": true});
            skArc(sketch, "E311.MirrorCS", {"start": v(29.89, -24.22) * mm, "mid": v(29.62, -23.88) * mm, "end": v(29.7, -23.46) * mm});
            skLineSegment(sketch, "E312.MirrorCS", {"start": v(37.09, -7.4) * mm, "end": v(37.32, -5.94) * mm, "construction": true});
            skArc(sketch, "E313.MirrorCS", {"start": v(-29.89, -24.22) * mm, "mid": v(-29.62, -23.88) * mm, "end": v(-29.7, -23.46) * mm});
            skArc(sketch, "E314.MirrorCS", {"start": v(9.96, -37.15) * mm, "mid": v(9.93, -36.72) * mm, "end": v(10.25, -36.43) * mm});
            skLineSegment(sketch, "E315.MirrorCS", {"start": v(4.47, -37.58) * mm, "end": v(7.4, -37.12) * mm});
            skArc(sketch, "E316.MirrorCS", {"start": v(-25.77, -28.56) * mm, "mid": v(-25.55, -28.2) * mm, "end": v(-25.7, -27.79) * mm});
            skLineSegment(sketch, "E317.MirrorCS", {"start": v(25.7, -27.79) * mm, "end": v(26.75, -26.74) * mm, "construction": true});
            skLineSegment(sketch, "E318.MirrorCS", {"start": v(-25.7, -27.79) * mm, "end": v(-26.75, -26.74) * mm, "construction": true});
            skLineSegment(sketch, "E319.MirrorCS", {"start": v(21.02, -31.48) * mm, "end": v(23.43, -29.73) * mm});
            skArc(sketch, "E320.MirrorCS", {"start": v(-31.44, -21.06) * mm, "mid": v(-31.82, -20.85) * mm, "end": v(-32.22, -21) * mm});
            skLineSegment(sketch, "E321.MirrorCS", {"start": v(29.7, -23.46) * mm, "end": v(30.57, -22.26) * mm, "construction": true});
            skArc(sketch, "E322.MirrorCS", {"start": v(34.36, -15.86) * mm, "mid": v(34.7, -15.6) * mm, "end": v(35.11, -15.68) * mm});
            skLineSegment(sketch, "E323.MirrorCS", {"start": v(32.73, -19.04) * mm, "end": v(34.63, -15.32) * mm, "construction": true});
            skLineSegment(sketch, "E324.MirrorCS", {"start": v(37.79, -1.48) * mm, "end": v(37.79, 0) * mm, "construction": true});
            skArc(sketch, "E325.MirrorCS", {"start": v(-20.97, -32.26) * mm, "mid": v(-20.81, -31.85) * mm, "end": v(-21.02, -31.48) * mm});
            skLineSegment(sketch, "E326.MirrorCS", {"start": v(29.7, -23.46) * mm, "end": v(31.44, -21.06) * mm});
            skArc(sketch, "E327.MirrorCS", {"start": v(14.38, -40.52) * mm, "mid": v(14.3, -40.86) * mm, "end": v(14.03, -41.07) * mm});
            skLineSegment(sketch, "E328.MirrorCS", {"start": v(-37.79, -1.48) * mm, "end": v(-37.79, 0) * mm, "construction": true});
            skLineSegment(sketch, "E329.MirrorCS", {"start": v(-15.3, -34.64) * mm, "end": v(-19.02, -32.74) * mm, "construction": true});
            skLineSegment(sketch, "E330.MirrorCS", {"start": v(15.84, -34.36) * mm, "end": v(17.16, -33.7) * mm, "construction": true});
            skLineSegment(sketch, "E331.MirrorCS", {"start": v(25.7, -27.79) * mm, "end": v(27.8, -25.69) * mm});
            skArc(sketch, "E332.MirrorCS", {"start": v(-15.66, -35.12) * mm, "mid": v(-15.57, -34.7) * mm, "end": v(-15.84, -34.36) * mm});
            skArc(sketch, "E333.MirrorCS", {"start": v(31.44, -21.06) * mm, "mid": v(31.82, -20.85) * mm, "end": v(32.22, -21) * mm});
            skLineSegment(sketch, "E334.MirrorCS", {"start": v(20.53, -31.84) * mm, "end": v(23.91, -29.38) * mm, "construction": true});
            skLineSegment(sketch, "E335.MirrorCS", {"start": v(12.74, -41.5) * mm, "end": v(14.03, -41.07) * mm});
            skLineSegment(sketch, "E336.MirrorCS", {"start": v(21.02, -31.48) * mm, "end": v(22.22, -30.6) * mm, "construction": true});
            skArc(sketch, "E337.MirrorCS", {"start": v(35.45, -24.34) * mm, "mid": v(35.59, -24.66) * mm, "end": v(35.5, -25) * mm});
            skLineSegment(sketch, "E338.MirrorCS", {"start": v(29.34, -23.95) * mm, "end": v(31.8, -20.57) * mm, "construction": true});
            skLineSegment(sketch, "E339.MirrorCS", {"start": v(3.87, -37.68) * mm, "end": v(8, -37.02) * mm, "construction": true});
            skArc(sketch, "E340.MirrorCS", {"start": v(15.66, -35.12) * mm, "mid": v(15.57, -34.7) * mm, "end": v(15.84, -34.36) * mm});
            skLineSegment(sketch, "E341.MirrorCS", {"start": v(-29.34, -23.95) * mm, "end": v(-31.8, -20.57) * mm, "construction": true});
            skLineSegment(sketch, "E342.MirrorCS", {"start": v(-25.7, -27.79) * mm, "end": v(-27.8, -25.69) * mm});
            skArc(sketch, "E343.MirrorCS", {"start": v(27.8, -25.69) * mm, "mid": v(28.2, -25.54) * mm, "end": v(28.58, -25.75) * mm});
            skLineSegment(sketch, "E344.MirrorCS", {"start": v(-25.27, -28.22) * mm, "end": v(-28.23, -25.26) * mm, "construction": true});
            skLineSegment(sketch, "E345.MirrorCS", {"start": v(-4.47, -37.58) * mm, "end": v(-7.4, -37.12) * mm});
            skLineSegment(sketch, "E346.MirrorCS", {"start": v(24.96, -35.53) * mm, "end": v(26.06, -34.73) * mm});
            skArc(sketch, "E347.MirrorCS", {"start": v(-33.31, -19.22) * mm, "mid": v(-33, -18.93) * mm, "end": v(-33, -18.5) * mm});
            skArc(sketch, "E348.MirrorCS", {"start": v(-27.8, -25.69) * mm, "mid": v(-28.2, -25.54) * mm, "end": v(-28.58, -25.75) * mm});
            skLineSegment(sketch, "E349.MirrorCS", {"start": v(-15.84, -34.36) * mm, "end": v(-17.16, -33.7) * mm, "construction": true});
            skArc(sketch, "E350.MirrorCS", {"start": v(34.7, -26.1) * mm, "mid": v(34.4, -26.29) * mm, "end": v(34.06, -26.25) * mm});
            skLineSegment(sketch, "E351.MirrorCS", {"start": v(-33, -18.5) * mm, "end": v(-33.68, -17.18) * mm, "construction": true});
            skArc(sketch, "E352.MirrorCS", {"start": v(7.4, -37.12) * mm, "mid": v(7.82, -37.23) * mm, "end": v(8, -37.63) * mm});
            skLineSegment(sketch, "E353.MirrorCS", {"start": v(-29.7, -23.46) * mm, "end": v(-31.44, -21.06) * mm});
            skLineSegment(sketch, "E354.MirrorCS", {"start": v(-33, -18.5) * mm, "end": v(-34.36, -15.86) * mm});
            skArc(sketch, "E355.MirrorCS", {"start": v(20.97, -32.26) * mm, "mid": v(20.81, -31.85) * mm, "end": v(21.02, -31.48) * mm});
            skLineSegment(sketch, "E356.MirrorCS", {"start": v(15.84, -34.36) * mm, "end": v(18.49, -33.02) * mm});
            skArc(sketch, "E357.MirrorCS", {"start": v(-38.38, -1.99) * mm, "mid": v(-37.97, -1.87) * mm, "end": v(-37.79, -1.48) * mm});
            skLineSegment(sketch, "E358.MirrorCS", {"start": v(25.27, -28.22) * mm, "end": v(28.23, -25.26) * mm, "construction": true});
            skArc(sketch, "E359.MirrorCS", {"start": v(24.96, -35.53) * mm, "mid": v(24.62, -35.62) * mm, "end": v(24.3, -35.48) * mm});
            skLineSegment(sketch, "E360.MirrorCS", {"start": v(19.1, -38.98) * mm, "end": v(20.3, -38.36) * mm});
            skArc(sketch, "E361.MirrorCS", {"start": v(-35.9, -13.73) * mm, "mid": v(-35.54, -13.5) * mm, "end": v(-35.5, -13.07) * mm});
            skArc(sketch, "E362.MirrorCS", {"start": v(-9.96, -37.15) * mm, "mid": v(-9.93, -36.72) * mm, "end": v(-10.25, -36.43) * mm});
            skArc(sketch, "E363.MirrorCS", {"start": v(23.43, -29.73) * mm, "mid": v(23.85, -29.65) * mm, "end": v(24.18, -29.92) * mm});
            skArc(sketch, "E364.MirrorCS", {"start": v(19.1, -38.98) * mm, "mid": v(18.75, -39.02) * mm, "end": v(18.46, -38.83) * mm});
            skLineSegment(sketch, "E365.MirrorCS", {"start": v(-15.84, -34.36) * mm, "end": v(-18.49, -33.02) * mm});
            skLineSegment(sketch, "E366.MirrorCS", {"start": v(-10.25, -36.43) * mm, "end": v(-11.66, -35.97) * mm, "construction": true});
            skLineSegment(sketch, "E367.MirrorCS", {"start": v(-35.5, -13.07) * mm, "end": v(-35.95, -11.66) * mm, "construction": true});
            skArc(sketch, "E368.MirrorCS", {"start": v(26.22, -34.1) * mm, "mid": v(26.25, -34.44) * mm, "end": v(26.06, -34.73) * mm});
            skArc(sketch, "E369.MirrorCS", {"start": v(-18.49, -33.02) * mm, "mid": v(-18.91, -33) * mm, "end": v(-19.2, -33.32) * mm});
            skArc(sketch, "E370.MirrorCS", {"start": v(20.56, -37.76) * mm, "mid": v(20.54, -38.1) * mm, "end": v(20.3, -38.36) * mm});
            skLineSegment(sketch, "E371.MirrorCS", {"start": v(34.7, -26.1) * mm, "end": v(35.5, -25) * mm});
            skArc(sketch, "E372.MirrorCS", {"start": v(-26.22, -34.1) * mm, "mid": v(-26.25, -34.44) * mm, "end": v(-26.06, -34.73) * mm});
            skLineSegment(sketch, "E373.MirrorCS", {"start": v(35.5, -13.07) * mm, "end": v(36.4, -10.25) * mm});
            skLineSegment(sketch, "E374.MirrorCS", {"start": v(-21.02, -31.48) * mm, "end": v(-23.43, -29.73) * mm});
            skLineSegment(sketch, "E375.MirrorCS", {"start": v(9.67, -36.62) * mm, "end": v(13.65, -35.32) * mm, "construction": true});
            skLineSegment(sketch, "E376.MirrorCS", {"start": v(38.82, -18.47) * mm, "end": v(35.11, -15.68) * mm});
            skLineSegment(sketch, "E377.MirrorCS", {"start": v(-32.73, -19.04) * mm, "end": v(-34.63, -15.32) * mm, "construction": true});
            skArc(sketch, "E378.MirrorCS", {"start": v(31.24, -29.56) * mm, "mid": v(31.33, -29.9) * mm, "end": v(31.18, -30.2) * mm});
            skLineSegment(sketch, "E379.MirrorCS", {"start": v(38.35, -20.32) * mm, "end": v(38.97, -19.11) * mm});
            skArc(sketch, "E380.MirrorCS", {"start": v(-23.43, -29.73) * mm, "mid": v(-23.85, -29.65) * mm, "end": v(-24.18, -29.92) * mm});
            skLineSegment(sketch, "E381.MirrorCS", {"start": v(41.05, -14.03) * mm, "end": v(41.47, -12.74) * mm});
            skLineSegment(sketch, "E382.MirrorCS", {"start": v(10.25, -36.43) * mm, "end": v(13.07, -35.51) * mm});
            skLineSegment(sketch, "E383.MirrorCS", {"start": v(15.3, -34.64) * mm, "end": v(19.02, -32.74) * mm, "construction": true});
            skArc(sketch, "E384.MirrorCS", {"start": v(30.22, -31.17) * mm, "mid": v(29.9, -31.32) * mm, "end": v(29.57, -31.23) * mm});
            skLineSegment(sketch, "E385.MirrorCS", {"start": v(-3.87, -37.68) * mm, "end": v(-8, -37.02) * mm, "construction": true});
            skArc(sketch, "E386.MirrorCS", {"start": v(-41.05, -14.03) * mm, "mid": v(-40.84, -14.3) * mm, "end": v(-40.5, -14.38) * mm});
            skArc(sketch, "E387.MirrorCS", {"start": v(-34.7, -26.1) * mm, "mid": v(-34.4, -26.29) * mm, "end": v(-34.06, -26.25) * mm});
            skLineSegment(sketch, "E388.MirrorCS", {"start": v(-37.09, -7.4) * mm, "end": v(-37.55, -4.47) * mm});
            skLineSegment(sketch, "E389.MirrorCS", {"start": v(-10.25, -36.43) * mm, "end": v(-13.07, -35.51) * mm});
            skArc(sketch, "E390.MirrorCS", {"start": v(42.6, -5.58) * mm, "mid": v(42.88, -5.8) * mm, "end": v(42.95, -6.14) * mm});
            skArc(sketch, "E391.MirrorCS", {"start": v(-37.55, -4.47) * mm, "mid": v(-37.8, -4.11) * mm, "end": v(-38.22, -4.07) * mm});
            skArc(sketch, "E392.MirrorCS", {"start": v(-13.07, -35.51) * mm, "mid": v(-13.5, -35.56) * mm, "end": v(-13.73, -35.92) * mm});
            skArc(sketch, "E393.MirrorCS", {"start": v(18.49, -33.02) * mm, "mid": v(18.91, -33) * mm, "end": v(19.2, -33.32) * mm});
            skLineSegment(sketch, "E394.MirrorCS", {"start": v(30.22, -31.17) * mm, "end": v(31.18, -30.2) * mm});
            skLineSegment(sketch, "E395.MirrorCS", {"start": v(-9.67, -36.62) * mm, "end": v(-13.65, -35.32) * mm, "construction": true});
            skLineSegment(sketch, "E396.MirrorCS", {"start": v(-24.96, -35.53) * mm, "end": v(-26.06, -34.73) * mm});
            skLineSegment(sketch, "E397.MirrorCS", {"start": v(6.14, -42.97) * mm, "end": v(7.48, -42.76) * mm});
            skLineSegment(sketch, "E398.MirrorCS", {"start": v(43.37, -0.68) * mm, "end": v(43.37, 0.68) * mm});
            skArc(sketch, "E399.MirrorCS", {"start": v(41.05, -14.03) * mm, "mid": v(40.84, -14.3) * mm, "end": v(40.5, -14.38) * mm});
            skLineSegment(sketch, "E400.MirrorCS", {"start": v(-34.7, -26.1) * mm, "end": v(-35.5, -25) * mm});
            skArc(sketch, "E401.MirrorCS", {"start": v(-38.82, -18.47) * mm, "mid": v(-39.01, -18.77) * mm, "end": v(-38.97, -19.11) * mm});
            skLineSegment(sketch, "E402.MirrorCS", {"start": v(-38.35, -20.32) * mm, "end": v(-38.97, -19.11) * mm});
            skArc(sketch, "E403.MirrorCS", {"start": v(38.35, -20.32) * mm, "mid": v(38.1, -20.56) * mm, "end": v(37.75, -20.58) * mm});
            skArc(sketch, "E404.MirrorCS", {"start": v(13.07, -35.51) * mm, "mid": v(13.5, -35.56) * mm, "end": v(13.73, -35.92) * mm});
            skArc(sketch, "E405.MirrorCS", {"start": v(41.23, -12.14) * mm, "mid": v(41.46, -12.4) * mm, "end": v(41.47, -12.74) * mm});
            skLineSegment(sketch, "E406.MirrorCS", {"start": v(-43.37, -0.68) * mm, "end": v(-43.37, 0.68) * mm});
            skArc(sketch, "E407.MirrorCS", {"start": v(-41.23, -12.14) * mm, "mid": v(-41.46, -12.4) * mm, "end": v(-41.47, -12.74) * mm});
            skArc(sketch, "E408.MirrorCS", {"start": v(-34.36, -15.86) * mm, "mid": v(-34.7, -15.6) * mm, "end": v(-35.11, -15.68) * mm});
            skArc(sketch, "E409.MirrorCS", {"start": v(43.37, -0.68) * mm, "mid": v(43.25, -1) * mm, "end": v(42.95, -1.18) * mm});
            skArc(sketch, "E410.MirrorCS", {"start": v(36.4, -10.25) * mm, "mid": v(36.7, -9.93) * mm, "end": v(37.13, -9.96) * mm});
            skArc(sketch, "E411.MirrorCS", {"start": v(38.82, -18.47) * mm, "mid": v(39.01, -18.77) * mm, "end": v(38.97, -19.11) * mm});
            skLineSegment(sketch, "E412.MirrorCS", {"start": v(35.45, -24.34) * mm, "end": v(32.22, -21) * mm});
            skArc(sketch, "E413.MirrorCS", {"start": v(-7.4, -37.12) * mm, "mid": v(-7.82, -37.23) * mm, "end": v(-8, -37.63) * mm});
            skLineSegment(sketch, "E414.MirrorCS", {"start": v(-20.53, -31.84) * mm, "end": v(-23.91, -29.38) * mm, "construction": true});
            skLineSegment(sketch, "E415.MirrorCS", {"start": v(37.79, -1.48) * mm, "end": v(37.79, 1.49) * mm});
            skArc(sketch, "E416.MirrorCS", {"start": v(-31.24, -29.56) * mm, "mid": v(-31.33, -29.9) * mm, "end": v(-31.18, -30.2) * mm});
            skArc(sketch, "E417.MirrorCS", {"start": v(6.14, -42.97) * mm, "mid": v(5.8, -42.9) * mm, "end": v(5.58, -42.64) * mm});
            skArc(sketch, "E418.MirrorCS", {"start": v(-43.37, -0.68) * mm, "mid": v(-43.25, -1) * mm, "end": v(-42.95, -1.18) * mm});
            skLineSegment(sketch, "E419.MirrorCS", {"start": v(-30.22, -31.17) * mm, "end": v(-31.18, -30.2) * mm});
            skArc(sketch, "E420.MirrorCS", {"start": v(-36.4, -10.25) * mm, "mid": v(-36.7, -9.93) * mm, "end": v(-37.13, -9.96) * mm});
            skLineSegment(sketch, "E421.MirrorCS", {"start": v(-37, -8) * mm, "end": v(-37.65, -3.87) * mm, "construction": true});
            skLineSegment(sketch, "E422.MirrorCS", {"start": v(-41.05, -14.03) * mm, "end": v(-41.47, -12.74) * mm});
            skArc(sketch, "E423.MirrorCS", {"start": v(-30.22, -31.17) * mm, "mid": v(-29.9, -31.32) * mm, "end": v(-29.57, -31.23) * mm});
            skArc(sketch, "E424.MirrorCS", {"start": v(-24.96, -35.53) * mm, "mid": v(-24.62, -35.62) * mm, "end": v(-24.3, -35.48) * mm});
            skArc(sketch, "E425.MirrorCS", {"start": v(-35.45, -24.34) * mm, "mid": v(-35.59, -24.66) * mm, "end": v(-35.5, -25) * mm});
            skLineSegment(sketch, "E426.MirrorCS", {"start": v(42.73, -7.48) * mm, "end": v(42.95, -6.14) * mm});
            skLineSegment(sketch, "E427.MirrorCS", {"start": v(-37.79, -1.48) * mm, "end": v(-37.79, 1.49) * mm});
            skArc(sketch, "E428.MirrorCS", {"start": v(-19.1, -38.98) * mm, "mid": v(-18.75, -39.02) * mm, "end": v(-18.46, -38.83) * mm});
            skLineSegment(sketch, "E429.MirrorCS", {"start": v(-41.23, -12.14) * mm, "end": v(-37.13, -9.96) * mm});
            skLineSegment(sketch, "E430.MirrorCS", {"start": v(-35.45, -24.34) * mm, "end": v(-32.22, -21) * mm});
            skLineSegment(sketch, "E431.MirrorCS", {"start": v(4.07, -38.25) * mm, "end": v(5.58, -42.64) * mm});
            skLineSegment(sketch, "E432.MirrorCS", {"start": v(-6.14, -42.97) * mm, "end": v(-7.48, -42.76) * mm});
            skLineSegment(sketch, "E433.MirrorCS", {"start": v(-42.73, -7.48) * mm, "end": v(-42.95, -6.14) * mm});
            skArc(sketch, "E434.MirrorCS", {"start": v(12.74, -41.5) * mm, "mid": v(12.4, -41.48) * mm, "end": v(12.13, -41.25) * mm});
            skArc(sketch, "E435.MirrorCS", {"start": v(-37.79, 1.49) * mm, "mid": v(-37.97, 1.88) * mm, "end": v(-38.38, 1.99) * mm});
            skArc(sketch, "E436.MirrorCS", {"start": v(-38.35, -20.32) * mm, "mid": v(-38.1, -20.56) * mm, "end": v(-37.75, -20.58) * mm});
            skArc(sketch, "E437.MirrorCS", {"start": v(-6.14, -42.97) * mm, "mid": v(-5.8, -42.9) * mm, "end": v(-5.58, -42.64) * mm});
            skArc(sketch, "E438.MirrorCS", {"start": v(-20.56, -37.76) * mm, "mid": v(-20.54, -38.1) * mm, "end": v(-20.3, -38.36) * mm});
            skLineSegment(sketch, "E439.MirrorCS", {"start": v(-37.79, -2.1) * mm, "end": v(-37.79, 2.1) * mm, "construction": true});
            skArc(sketch, "E440.MirrorCS", {"start": v(42.73, -7.48) * mm, "mid": v(42.56, -7.79) * mm, "end": v(42.24, -7.9) * mm});
            skLineSegment(sketch, "E441.MirrorCS", {"start": v(9.96, -37.15) * mm, "end": v(12.13, -41.25) * mm});
            skArc(sketch, "E442.MirrorCS", {"start": v(-7.91, -42.27) * mm, "mid": v(-7.79, -42.6) * mm, "end": v(-7.48, -42.76) * mm});
            skLineSegment(sketch, "E443.MirrorCS", {"start": v(37.79, -2.1) * mm, "end": v(37.79, 2.1) * mm, "construction": true});
            skLineSegment(sketch, "E444.MirrorCS", {"start": v(25.77, -28.56) * mm, "end": v(29.57, -31.23) * mm});
            skLineSegment(sketch, "E445.MirrorCS", {"start": v(-35.5, -13.07) * mm, "end": v(-36.4, -10.25) * mm});
            skLineSegment(sketch, "E446.MirrorCS", {"start": v(20.97, -32.26) * mm, "end": v(24.3, -35.48) * mm});
            skLineSegment(sketch, "E447.MirrorCS", {"start": v(-20.97, -32.26) * mm, "end": v(-24.3, -35.48) * mm});
            skArc(sketch, "E448.MirrorCS", {"start": v(-12.74, -41.5) * mm, "mid": v(-12.4, -41.48) * mm, "end": v(-12.13, -41.25) * mm});
            skLineSegment(sketch, "E449.MirrorCS", {"start": v(-9.96, -37.15) * mm, "end": v(-12.13, -41.25) * mm});
            skArc(sketch, "E450.MirrorCS", {"start": v(-42.6, -5.58) * mm, "mid": v(-42.88, -5.8) * mm, "end": v(-42.95, -6.14) * mm});
            skArc(sketch, "E451.MirrorCS", {"start": v(-42.95, 1.18) * mm, "mid": v(-43.25, 1) * mm, "end": v(-43.37, 0.68) * mm});
            skArc(sketch, "E452.MirrorCS", {"start": v(37.79, 1.49) * mm, "mid": v(37.97, 1.88) * mm, "end": v(38.38, 1.99) * mm});
            skLineSegment(sketch, "E453.MirrorCS", {"start": v(15.66, -35.12) * mm, "end": v(18.46, -38.83) * mm});
            skLineSegment(sketch, "E454.MirrorCS", {"start": v(-12.74, -41.5) * mm, "end": v(-14.03, -41.07) * mm});
            skLineSegment(sketch, "E455.MirrorCS", {"start": v(-19.1, -38.98) * mm, "end": v(-20.3, -38.36) * mm});
            skArc(sketch, "E456.MirrorCS", {"start": v(7.91, -42.27) * mm, "mid": v(7.79, -42.6) * mm, "end": v(7.48, -42.76) * mm});
            skArc(sketch, "E457.MirrorCS", {"start": v(42.95, 1.18) * mm, "mid": v(43.25, 1) * mm, "end": v(43.37, 0.68) * mm});
            skLineSegment(sketch, "E458.MirrorCS", {"start": v(-15.66, -35.12) * mm, "end": v(-18.46, -38.83) * mm});
            skArc(sketch, "E459.MirrorCS", {"start": v(-14.38, -40.52) * mm, "mid": v(-14.3, -40.86) * mm, "end": v(-14.03, -41.07) * mm});
            skArc(sketch, "E460.MirrorCS", {"start": v(-42.73, -7.48) * mm, "mid": v(-42.56, -7.79) * mm, "end": v(-42.24, -7.9) * mm});
            skLineSegment(sketch, "E461.MirrorCS", {"start": v(41.23, -12.14) * mm, "end": v(37.13, -9.96) * mm});
            skLineSegment(sketch, "E462.MirrorCS", {"start": v(31.24, -29.56) * mm, "end": v(28.58, -25.75) * mm});
            skLineSegment(sketch, "E463.MirrorCS", {"start": v(-4.07, -38.25) * mm, "end": v(-5.58, -42.64) * mm});
            skLineSegment(sketch, "E464.MirrorCS", {"start": v(1.99, -38.41) * mm, "end": v(1.18, -42.98) * mm});
            skLineSegment(sketch, "E465.MirrorCS", {"start": v(0, -43.4) * mm, "end": v(0, -37.82) * mm});
            skLineSegment(sketch, "E466.MirrorCS", {"start": v(-1.18, -42.98) * mm, "end": v(-1.99, -38.41) * mm});
            skLineSegment(sketch, "E467.MirrorCS", {"start": v(26.22, -34.1) * mm, "end": v(24.18, -29.92) * mm});
            skLineSegment(sketch, "E468.MirrorCS", {"start": v(29.89, -24.22) * mm, "end": v(34.06, -26.25) * mm});
            skLineSegment(sketch, "E469.MirrorCS", {"start": v(38.66, -19.72) * mm, "end": v(33.68, -17.18) * mm});
            skLineSegment(sketch, "E470.MirrorCS", {"start": v(-33.31, -19.22) * mm, "end": v(-37.75, -20.58) * mm});
            skPoint(sketch, "E471.MirrorP", {"position": v(14.44, -40.94) * mm});
            skPoint(sketch, "E472.MirrorP", {"position": v(26.4, -34.48) * mm});
            skPoint(sketch, "E473.MirrorP", {"position": v(35.74, -24.65) * mm});
            skLineSegment(sketch, "E474.MirrorCS", {"start": v(38.38, -1.99) * mm, "end": v(42.95, -1.18) * mm});
            skLineSegment(sketch, "E475.MirrorCS", {"start": v(1.18, -42.98) * mm, "end": v(1.99, -38.41) * mm});
            skLineSegment(sketch, "E476.MirrorCS", {"start": v(-1.99, -38.41) * mm, "end": v(-1.18, -42.98) * mm});
            skLineSegment(sketch, "E477.MirrorCS", {"start": v(42.84, -6.81) * mm, "end": v(37.32, -5.94) * mm});
            skLineSegment(sketch, "E478.MirrorCS", {"start": v(33.31, -19.22) * mm, "end": v(37.75, -20.58) * mm});
            skLineSegment(sketch, "E479.MirrorCS", {"start": v(-42.6, -5.58) * mm, "end": v(-38.22, -4.07) * mm});
            skLineSegment(sketch, "E480.MirrorCS", {"start": v(35.1, -25.54) * mm, "end": v(30.57, -22.26) * mm});
            skLineSegment(sketch, "E481.MirrorCS", {"start": v(35.9, -13.73) * mm, "end": v(40.5, -14.38) * mm});
            skLineSegment(sketch, "E482.MirrorCS", {"start": v(14.38, -40.52) * mm, "end": v(13.73, -35.92) * mm});
            skPoint(sketch, "E483.MirrorP", {"position": v(34.63, -15.32) * mm});
            skLineSegment(sketch, "E484.MirrorCS", {"start": v(-31.24, -29.56) * mm, "end": v(-28.58, -25.75) * mm});
            skPoint(sketch, "E485.MirrorP", {"position": v(37.65, -3.87) * mm});
            skPoint(sketch, "E486.MirrorP", {"position": v(28.23, -25.26) * mm});
            skLineSegment(sketch, "E487.MirrorCS", {"start": v(19.7, -38.67) * mm, "end": v(17.16, -33.7) * mm});
            skLineSegment(sketch, "E488.MirrorCS", {"start": v(-29.89, -24.22) * mm, "end": v(-34.06, -26.25) * mm});
            skPoint(sketch, "E489.MirrorP", {"position": v(1.1, -43.4) * mm});
            skPoint(sketch, "E490.MirrorP", {"position": v(32.73, -19.04) * mm});
            skPoint(sketch, "E491.MirrorP", {"position": v(37, -8) * mm});
            skPoint(sketch, "E492.MirrorP", {"position": v(3.87, -37.68) * mm});
            skLineSegment(sketch, "E493.MirrorCS", {"start": v(7.91, -42.27) * mm, "end": v(8, -37.63) * mm});
            skLineSegment(sketch, "E494.MirrorCS", {"start": v(30.7, -30.69) * mm, "end": v(26.75, -26.74) * mm});
            skPoint(sketch, "E495.MirrorP", {"position": v(-2.1, -37.82) * mm});
            skLineSegment(sketch, "E496.MirrorCS", {"start": v(42.95, 1.18) * mm, "end": v(38.38, 1.99) * mm});
            skPoint(sketch, "E497.MirrorP", {"position": v(35.3, -13.65) * mm});
            skPoint(sketch, "E498.MirrorP", {"position": v(29.34, -23.95) * mm});
            skPoint(sketch, "E499.MirrorP", {"position": v(2.1, -37.82) * mm});
            skLineSegment(sketch, "E500.MirrorCS", {"start": v(13.39, -41.28) * mm, "end": v(11.66, -35.97) * mm});
            skPoint(sketch, "E501.MirrorP", {"position": v(36.6, -9.67) * mm});
            skPoint(sketch, "E502.MirrorP", {"position": v(31.8, -20.57) * mm});
            skPoint(sketch, "E503.MirrorP", {"position": v(23.91, -29.38) * mm});
            skPoint(sketch, "E504.MirrorP", {"position": v(-1.1, -43.4) * mm});
            skLineSegment(sketch, "E505.MirrorCS", {"start": v(37.6, -8) * mm, "end": v(42.24, -7.9) * mm});
            skLineSegment(sketch, "E506.MirrorCS", {"start": v(-25.77, -28.56) * mm, "end": v(-29.57, -31.23) * mm});
            skLineSegment(sketch, "E507.MirrorCS", {"start": v(41.26, -13.39) * mm, "end": v(35.95, -11.66) * mm});
            skPoint(sketch, "E508.MirrorP", {"position": v(20.68, -38.17) * mm});
            skLineSegment(sketch, "E509.MirrorCS", {"start": v(6.81, -42.87) * mm, "end": v(5.94, -37.35) * mm});
            skLineSegment(sketch, "E510.MirrorCS", {"start": v(-38.66, -19.72) * mm, "end": v(-33.68, -17.18) * mm});
            skLineSegment(sketch, "E511.MirrorCS", {"start": v(42.6, -5.58) * mm, "end": v(38.22, -4.07) * mm});
            skLineSegment(sketch, "E512.MirrorCS", {"start": v(20.56, -37.76) * mm, "end": v(19.2, -33.32) * mm});
            skPoint(sketch, "E513.MirrorP", {"position": v(5.72, -43.04) * mm});
            skPoint(sketch, "E514.MirrorP", {"position": v(31.48, -29.9) * mm});
            skLineSegment(sketch, "E515.MirrorCS", {"start": v(-38.82, -18.47) * mm, "end": v(-35.11, -15.68) * mm});
            skPoint(sketch, "E516.MirrorP", {"position": v(39.16, -18.73) * mm});
            skPoint(sketch, "E517.MirrorP", {"position": v(43.01, -5.72) * mm});
            skLineSegment(sketch, "E518.MirrorCS", {"start": v(25.5, -35.13) * mm, "end": v(22.22, -30.6) * mm});
            skLineSegment(sketch, "E519.MirrorCS", {"start": v(-13.39, -41.28) * mm, "end": v(-11.66, -35.97) * mm});
            skPoint(sketch, "E520.MirrorP", {"position": v(41.6, -12.34) * mm});
            skPoint(sketch, "E521.MirrorP", {"position": v(-3.87, -37.68) * mm});
            skPoint(sketch, "E522.MirrorP", {"position": v(-37, -8) * mm});
            skPoint(sketch, "E523.MirrorP", {"position": v(-29.34, -23.95) * mm});
            skLineSegment(sketch, "E524.MirrorCS", {"start": v(-38.38, -1.99) * mm, "end": v(-42.95, -1.18) * mm});
            skLineSegment(sketch, "E525.MirrorCS", {"start": v(-37.6, -8) * mm, "end": v(-42.24, -7.9) * mm});
            skPoint(sketch, "E526.MirrorP", {"position": v(-26.4, -34.48) * mm});
            skPoint(sketch, "E527.MirrorP", {"position": v(-19.02, -32.74) * mm});
            skPoint(sketch, "E528.MirrorP", {"position": v(40.92, -14.44) * mm});
            skLineSegment(sketch, "E529.MirrorCS", {"start": v(-26.22, -34.1) * mm, "end": v(-24.18, -29.92) * mm});
            skLineSegment(sketch, "E530.MirrorCS", {"start": v(-6.81, -42.87) * mm, "end": v(-5.94, -37.35) * mm});
            skPoint(sketch, "E531.MirrorP", {"position": v(12.34, -41.63) * mm});
            skPoint(sketch, "E532.MirrorP", {"position": v(24.61, -35.78) * mm});
            skPoint(sketch, "E533.MirrorP", {"position": v(34.44, -26.44) * mm});
            skPoint(sketch, "E534.MirrorP", {"position": v(-14.44, -40.94) * mm});
            skPoint(sketch, "E535.MirrorP", {"position": v(-7.9, -42.7) * mm});
            skLineSegment(sketch, "E536.MirrorCS", {"start": v(-25.5, -35.13) * mm, "end": v(-22.22, -30.6) * mm});
            skPoint(sketch, "E537.MirrorP", {"position": v(-41.6, -12.34) * mm});
            skPoint(sketch, "E538.MirrorP", {"position": v(-38.16, -20.7) * mm});
            skPoint(sketch, "E539.MirrorP", {"position": v(-34.44, -26.44) * mm});
            skLineSegment(sketch, "E540.MirrorCS", {"start": v(-30.7, -30.69) * mm, "end": v(-26.75, -26.74) * mm});
            skPoint(sketch, "E541.MirrorP", {"position": v(8, -37.02) * mm});
            skPoint(sketch, "E542.MirrorP", {"position": v(19.02, -32.74) * mm});
            skPoint(sketch, "E543.MirrorP", {"position": v(-35.74, -24.65) * mm});
            skPoint(sketch, "E544.MirrorP", {"position": v(-29.92, -31.47) * mm});
            skPoint(sketch, "E545.MirrorP", {"position": v(-40.92, -14.44) * mm});
            skLineSegment(sketch, "E546.MirrorCS", {"start": v(-19.7, -38.67) * mm, "end": v(-17.16, -33.7) * mm});
            skPoint(sketch, "E547.MirrorP", {"position": v(-18.71, -39.17) * mm});
            skLineSegment(sketch, "E548.MirrorCS", {"start": v(-20.56, -37.76) * mm, "end": v(-19.2, -33.32) * mm});
            skLineSegment(sketch, "E549.MirrorCS", {"start": v(-41.26, -13.39) * mm, "end": v(-35.95, -11.66) * mm});
            skPoint(sketch, "E550.MirrorP", {"position": v(15.3, -34.64) * mm});
            skPoint(sketch, "E551.MirrorP", {"position": v(25.27, -28.22) * mm});
            skPoint(sketch, "E552.MirrorP", {"position": v(-35.3, -13.65) * mm});
            skPoint(sketch, "E553.MirrorP", {"position": v(-5.72, -43.04) * mm});
            skPoint(sketch, "E554.MirrorP", {"position": v(-25.27, -28.22) * mm});
            skLineSegment(sketch, "E555.MirrorCS", {"start": v(-14.38, -40.52) * mm, "end": v(-13.73, -35.92) * mm});
            skPoint(sketch, "E556.MirrorP", {"position": v(-20.68, -38.17) * mm});
            skPoint(sketch, "E557.MirrorP", {"position": v(-9.67, -36.62) * mm});
            skPoint(sketch, "E558.MirrorP", {"position": v(-32.73, -19.04) * mm});
            skPoint(sketch, "E559.MirrorP", {"position": v(20.53, -31.84) * mm});
            skPoint(sketch, "E560.MirrorP", {"position": v(9.67, -36.62) * mm});
            skPoint(sketch, "E561.MirrorP", {"position": v(-13.65, -35.32) * mm});
            skLineSegment(sketch, "E562.MirrorCS", {"start": v(-42.95, 1.18) * mm, "end": v(-38.38, 1.99) * mm});
            skPoint(sketch, "E563.MirrorP", {"position": v(-20.53, -31.84) * mm});
            skPoint(sketch, "E564.MirrorP", {"position": v(-39.16, -18.73) * mm});
            skPoint(sketch, "E565.MirrorP", {"position": v(-24.61, -35.78) * mm});
            skPoint(sketch, "E566.MirrorP", {"position": v(-23.91, -29.38) * mm});
            skPoint(sketch, "E567.MirrorP", {"position": v(13.65, -35.32) * mm});
            skPoint(sketch, "E568.MirrorP", {"position": v(-36.6, -9.67) * mm});
            skLineSegment(sketch, "E569.MirrorCS", {"start": v(-7.91, -42.27) * mm, "end": v(-8, -37.63) * mm});
            skPoint(sketch, "E570.MirrorP", {"position": v(-31.48, -29.9) * mm});
            skPoint(sketch, "E571.MirrorP", {"position": v(-37.65, -3.87) * mm});
            skPoint(sketch, "E572.MirrorP", {"position": v(-28.23, -25.26) * mm});
            skLineSegment(sketch, "E573.MirrorCS", {"start": v(-42.84, -6.81) * mm, "end": v(-37.32, -5.94) * mm});
            skPoint(sketch, "E574.MirrorP", {"position": v(-43.01, -5.72) * mm});
            skLineSegment(sketch, "E575.MirrorCS", {"start": v(-35.1, -25.54) * mm, "end": v(-30.57, -22.26) * mm});
            skPoint(sketch, "E576.MirrorP", {"position": v(-31.8, -20.57) * mm});
            skPoint(sketch, "E577.MirrorP", {"position": v(-34.63, -15.32) * mm});
            skPoint(sketch, "E578.MirrorP", {"position": v(-15.3, -34.64) * mm});
            skLineSegment(sketch, "E579.MirrorCS", {"start": v(-35.9, -13.73) * mm, "end": v(-40.5, -14.38) * mm});
            skPoint(sketch, "E580.MirrorP", {"position": v(-42.67, -7.9) * mm});
            skPoint(sketch, "E581.MirrorP", {"position": v(42.67, -7.9) * mm});
            skPoint(sketch, "E582.MirrorP", {"position": v(-12.34, -41.63) * mm});
            skPoint(sketch, "E583.MirrorP", {"position": v(-8, -37.02) * mm});
            skPoint(sketch, "E584.MirrorP", {"position": v(18.71, -39.17) * mm});
            skPoint(sketch, "E585.MirrorP", {"position": v(29.92, -31.47) * mm});
            skPoint(sketch, "E586.MirrorP", {"position": v(7.9, -42.7) * mm});
            skPoint(sketch, "E587.MirrorP", {"position": v(38.16, -20.7) * mm});
            skSolve(sketch);
        }
        {
            var Q0;
            Q0=qCreatedBy(makeId("Front.planeOp"),FACE);
            var sketch = newSketch(context, id + "F4", { "sketchPlane" : qUnion([Q0])});
            skArc(sketch, "E588.MirrorCS", {"start": v(-103.64, 21.15) * mm, "mid": v(-103.75, 20.73) * mm, "end": v(-104.14, 20.55) * mm});
            skLineSegment(sketch, "E589.MirrorCS", {"start": v(-104.14, 20.55) * mm, "end": v(-105.63, 20.55) * mm, "construction": true});
            skLineSegment(sketch, "E590.MirrorCS", {"start": v(-104.14, 20.55) * mm, "end": v(-107.11, 20.55) * mm});
            skLineSegment(sketch, "E591.MirrorCS", {"start": v(-103.53, 20.55) * mm, "end": v(-107.72, 20.55) * mm, "construction": true});
            skArc(sketch, "E592.MirrorCS", {"start": v(-107.11, 20.55) * mm, "mid": v(-107.5, 20.73) * mm, "end": v(-107.62, 21.15) * mm});
            skLineSegment(sketch, "E593.MirrorCS", {"start": v(-104.95, 26.14) * mm, "end": v(-106.3, 26.14) * mm});
            skArc(sketch, "E594.MirrorCS", {"start": v(-106.8, 25.72) * mm, "mid": v(-106.63, 26.03) * mm, "end": v(-106.3, 26.14) * mm});
            skArc(sketch, "E595.MirrorCS", {"start": v(-104.95, 26.14) * mm, "mid": v(-104.62, 26.03) * mm, "end": v(-104.44, 25.72) * mm});
            skLineSegment(sketch, "E596.MirrorCS", {"start": v(-103.64, 21.15) * mm, "end": v(-104.44, 25.72) * mm});
            skLineSegment(sketch, "E597.MirrorCS", {"start": v(-106.8, 25.72) * mm, "end": v(-107.62, 21.15) * mm});
            skPoint(sketch, "E598.MirrorP", {"position": v(-107.72, 20.55) * mm});
            skPoint(sketch, "E599.MirrorP", {"position": v(-103.53, 20.55) * mm});
            skPoint(sketch, "E600.MirrorP", {"position": v(-104.52, 26.14) * mm});
            skPoint(sketch, "E601.MirrorP", {"position": v(-106.73, 26.14) * mm});
            skArc(sketch, "E602.MirrorCS", {"start": v(-109.7, 20.8) * mm, "mid": v(-109.68, 20.37) * mm, "end": v(-110, 20.08) * mm});
            skLineSegment(sketch, "E603.MirrorCS", {"start": v(-110, 20.08) * mm, "end": v(-111.41, 19.62) * mm, "construction": true});
            skLineSegment(sketch, "E604.MirrorCS", {"start": v(-110, 20.08) * mm, "end": v(-112.83, 19.16) * mm});
            skLineSegment(sketch, "E605.MirrorCS", {"start": v(-109.42, 20.27) * mm, "end": v(-113.4, 18.97) * mm, "construction": true});
            skArc(sketch, "E606.MirrorCS", {"start": v(-112.83, 19.16) * mm, "mid": v(-113.25, 19.21) * mm, "end": v(-113.49, 19.57) * mm});
            skLineSegment(sketch, "E607.MirrorCS", {"start": v(-112.5, 25.15) * mm, "end": v(-113.79, 24.73) * mm});
            skArc(sketch, "E608.MirrorCS", {"start": v(-114.14, 24.18) * mm, "mid": v(-114.06, 24.52) * mm, "end": v(-113.79, 24.73) * mm});
            skArc(sketch, "E609.MirrorCS", {"start": v(-112.5, 25.15) * mm, "mid": v(-112.15, 25.14) * mm, "end": v(-111.89, 24.9) * mm});
            skLineSegment(sketch, "E610.MirrorCS", {"start": v(-109.7, 20.8) * mm, "end": v(-111.89, 24.9) * mm});
            skLineSegment(sketch, "E611.MirrorCS", {"start": v(-114.14, 24.18) * mm, "end": v(-113.49, 19.57) * mm});
            skPoint(sketch, "E612.MirrorP", {"position": v(-113.4, 18.97) * mm});
            skPoint(sketch, "E613.MirrorP", {"position": v(-109.42, 20.27) * mm});
            skPoint(sketch, "E614.MirrorP", {"position": v(-112.09, 25.29) * mm});
            skPoint(sketch, "E615.MirrorP", {"position": v(-114.2, 24.6) * mm});
            skArc(sketch, "E616.MirrorCS", {"start": v(-92.64, 16.23) * mm, "mid": v(-92.97, 15.96) * mm, "end": v(-93.4, 16.04) * mm});
            skLineSegment(sketch, "E617.MirrorCS", {"start": v(-93.4, 16.04) * mm, "end": v(-94.6, 16.92) * mm, "construction": true});
            skLineSegment(sketch, "E618.MirrorCS", {"start": v(-93.4, 16.04) * mm, "end": v(-95.8, 17.8) * mm});
            skLineSegment(sketch, "E619.MirrorCS", {"start": v(-92.9, 15.69) * mm, "end": v(-96.3, 18.16) * mm, "construction": true});
            skArc(sketch, "E620.MirrorCS", {"start": v(-95.8, 17.8) * mm, "mid": v(-96, 18.17) * mm, "end": v(-95.85, 18.57) * mm});
            skLineSegment(sketch, "E621.MirrorCS", {"start": v(-90.75, 21.04) * mm, "end": v(-91.85, 21.84) * mm});
            skArc(sketch, "E622.MirrorCS", {"start": v(-92.5, 21.8) * mm, "mid": v(-92.19, 21.94) * mm, "end": v(-91.85, 21.84) * mm});
            skArc(sketch, "E623.MirrorCS", {"start": v(-90.75, 21.04) * mm, "mid": v(-90.56, 20.75) * mm, "end": v(-90.6, 20.4) * mm});
            skLineSegment(sketch, "E624.MirrorCS", {"start": v(-92.64, 16.23) * mm, "end": v(-90.6, 20.4) * mm});
            skLineSegment(sketch, "E625.MirrorCS", {"start": v(-92.5, 21.8) * mm, "end": v(-95.85, 18.57) * mm});
            skPoint(sketch, "E626.MirrorP", {"position": v(-96.3, 18.16) * mm});
            skLineSegment(sketch, "E627.MirrorCS", {"start": v(-91.3, 21.44) * mm, "end": v(-94.6, 16.92) * mm});
            skPoint(sketch, "E628.MirrorP", {"position": v(-92.9, 15.69) * mm});
            skPoint(sketch, "E629.MirrorP", {"position": v(-90.4, 20.8) * mm});
            skPoint(sketch, "E630.MirrorP", {"position": v(-92.2, 22.1) * mm});
            skArc(sketch, "E631.MirrorCS", {"start": v(-97.74, 19.53) * mm, "mid": v(-97.98, 19.17) * mm, "end": v(-98.4, 19.12) * mm});
            skLineSegment(sketch, "E632.MirrorCS", {"start": v(-98.4, 19.12) * mm, "end": v(-99.82, 19.58) * mm, "construction": true});
            skLineSegment(sketch, "E633.MirrorCS", {"start": v(-98.4, 19.12) * mm, "end": v(-101.23, 20.04) * mm});
            skLineSegment(sketch, "E634.MirrorCS", {"start": v(-97.83, 18.93) * mm, "end": v(-101.81, 20.23) * mm, "construction": true});
            skArc(sketch, "E635.MirrorCS", {"start": v(-101.23, 20.04) * mm, "mid": v(-101.55, 20.33) * mm, "end": v(-101.53, 20.76) * mm});
            skLineSegment(sketch, "E636.MirrorCS", {"start": v(-97.44, 24.69) * mm, "end": v(-98.73, 25.11) * mm});
            skArc(sketch, "E637.MirrorCS", {"start": v(-99.34, 24.87) * mm, "mid": v(-99.08, 25.1) * mm, "end": v(-98.73, 25.11) * mm});
            skArc(sketch, "E638.MirrorCS", {"start": v(-97.44, 24.69) * mm, "mid": v(-97.16, 24.47) * mm, "end": v(-97.1, 24.13) * mm});
            skLineSegment(sketch, "E639.MirrorCS", {"start": v(-97.74, 19.53) * mm, "end": v(-97.1, 24.13) * mm});
            skLineSegment(sketch, "E640.MirrorCS", {"start": v(-99.34, 24.87) * mm, "end": v(-101.53, 20.76) * mm});
            skPoint(sketch, "E641.MirrorP", {"position": v(-101.81, 20.23) * mm});
            skLineSegment(sketch, "E642.MirrorCS", {"start": v(-98.08, 24.9) * mm, "end": v(-99.82, 19.58) * mm});
            skPoint(sketch, "E643.MirrorP", {"position": v(-97.83, 18.93) * mm});
            skPoint(sketch, "E644.MirrorP", {"position": v(-97.03, 24.56) * mm});
            skPoint(sketch, "E645.MirrorP", {"position": v(-99.14, 25.24) * mm});
            skArc(sketch, "E646.MirrorCS", {"start": v(-97.53, -21.22) * mm, "mid": v(-97.26, -21) * mm, "end": v(-97.19, -20.66) * mm});
            skLineSegment(sketch, "E647.MirrorCS", {"start": v(-93.45, -12.6) * mm, "end": v(-95.87, -14.33) * mm});
            skLineSegment(sketch, "E648.MirrorCS", {"start": v(-93.45, -12.6) * mm, "end": v(-94.66, -13.46) * mm, "construction": true});
            skLineSegment(sketch, "E649.MirrorCS", {"start": v(-98.48, -15.64) * mm, "end": v(-101.31, -16.56) * mm});
            skArc(sketch, "E650.MirrorCS", {"start": v(-95.87, -14.33) * mm, "mid": v(-96.08, -14.7) * mm, "end": v(-95.92, -15.11) * mm});
            skArc(sketch, "E651.MirrorCS", {"start": v(-92.7, -12.78) * mm, "mid": v(-93.03, -12.51) * mm, "end": v(-93.45, -12.6) * mm});
            skLineSegment(sketch, "E652.MirrorCS", {"start": v(-97.53, -21.22) * mm, "end": v(-98.83, -21.64) * mm});
            skLineSegment(sketch, "E653.MirrorCS", {"start": v(-92.96, -12.24) * mm, "end": v(-96.36, -14.7) * mm, "construction": true});
            skArc(sketch, "E654.MirrorCS", {"start": v(-97.82, -16.06) * mm, "mid": v(-98.05, -15.7) * mm, "end": v(-98.48, -15.64) * mm});
            skArc(sketch, "E655.MirrorCS", {"start": v(-92.59, -18.35) * mm, "mid": v(-92.27, -18.5) * mm, "end": v(-91.94, -18.4) * mm});
            skArc(sketch, "E656.MirrorCS", {"start": v(-101.31, -16.56) * mm, "mid": v(-101.63, -16.85) * mm, "end": v(-101.6, -17.28) * mm});
            skArc(sketch, "E657.MirrorCS", {"start": v(-90.83, -17.6) * mm, "mid": v(-90.64, -17.31) * mm, "end": v(-90.67, -16.97) * mm});
            skArc(sketch, "E658.MirrorCS", {"start": v(-99.44, -21.39) * mm, "mid": v(-99.18, -21.62) * mm, "end": v(-98.83, -21.64) * mm});
            skLineSegment(sketch, "E659.MirrorCS", {"start": v(-90.83, -17.6) * mm, "end": v(-91.94, -18.4) * mm});
            skLineSegment(sketch, "E660.MirrorCS", {"start": v(-97.9, -15.46) * mm, "end": v(-101.89, -16.74) * mm, "construction": true});
            skPoint(sketch, "E661.MirrorP", {"position": v(-101.89, -16.74) * mm});
            skLineSegment(sketch, "E662.MirrorCS", {"start": v(-99.44, -21.39) * mm, "end": v(-101.6, -17.28) * mm});
            skLineSegment(sketch, "E663.MirrorCS", {"start": v(-97.82, -16.06) * mm, "end": v(-97.19, -20.66) * mm});
            skPoint(sketch, "E664.MirrorP", {"position": v(-97.13, -21.09) * mm});
            skPoint(sketch, "E665.MirrorP", {"position": v(-92.28, -18.65) * mm});
            skLineSegment(sketch, "E666.MirrorCS", {"start": v(-98.48, -15.64) * mm, "end": v(-99.9, -16.1) * mm, "construction": true});
            skLineSegment(sketch, "E667.MirrorCS", {"start": v(-92.59, -18.35) * mm, "end": v(-95.92, -15.11) * mm});
            skPoint(sketch, "E668.MirrorP", {"position": v(-97.9, -15.46) * mm});
            skPoint(sketch, "E669.MirrorP", {"position": v(-92.96, -12.24) * mm});
            skPoint(sketch, "E670.MirrorP", {"position": v(-96.36, -14.7) * mm});
            skPoint(sketch, "E671.MirrorP", {"position": v(-90.49, -17.35) * mm});
            skLineSegment(sketch, "E672.MirrorCS", {"start": v(-92.7, -12.78) * mm, "end": v(-90.67, -16.97) * mm});
            skPoint(sketch, "E673.MirrorP", {"position": v(-103.61, -17.05) * mm});
            skLineSegment(sketch, "E674.MirrorCS", {"start": v(-98.18, -21.43) * mm, "end": v(-99.9, -16.1) * mm});
            skLineSegment(sketch, "E675.MirrorCS", {"start": v(-91.38, -18) * mm, "end": v(-94.66, -13.46) * mm});
            skPoint(sketch, "E676.MirrorP", {"position": v(-99.24, -21.77) * mm});
            skArc(sketch, "E677.MirrorCS", {"start": v(-113.59, -16.03) * mm, "mid": v(-113.35, -15.67) * mm, "end": v(-112.93, -15.61) * mm});
            skLineSegment(sketch, "E678.MirrorCS", {"start": v(-112.93, -15.61) * mm, "end": v(-110.1, -16.54) * mm});
            skLineSegment(sketch, "E679.MirrorCS", {"start": v(-117.94, -12.54) * mm, "end": v(-116.74, -13.42) * mm, "construction": true});
            skLineSegment(sketch, "E680.MirrorCS", {"start": v(-112.93, -15.61) * mm, "end": v(-111.51, -16.07) * mm, "construction": true});
            skArc(sketch, "E681.MirrorCS", {"start": v(-115.53, -14.3) * mm, "mid": v(-115.32, -14.67) * mm, "end": v(-115.48, -15.07) * mm});
            skLineSegment(sketch, "E682.MirrorCS", {"start": v(-118.43, -12.18) * mm, "end": v(-115.04, -14.65) * mm, "construction": true});
            skArc(sketch, "E683.MirrorCS", {"start": v(-118.7, -12.73) * mm, "mid": v(-118.36, -12.46) * mm, "end": v(-117.94, -12.54) * mm});
            skLineSegment(sketch, "E684.MirrorCS", {"start": v(-117.94, -12.54) * mm, "end": v(-115.53, -14.3) * mm});
            skArc(sketch, "E685.MirrorCS", {"start": v(-118.63, 16.29) * mm, "mid": v(-118.3, 16.02) * mm, "end": v(-117.88, 16.1) * mm});
            skArc(sketch, "E686.MirrorCS", {"start": v(-110.1, -16.54) * mm, "mid": v(-109.78, -16.83) * mm, "end": v(-109.8, -17.26) * mm});
            skLineSegment(sketch, "E687.MirrorCS", {"start": v(-113.5, -15.43) * mm, "end": v(-109.52, -16.72) * mm, "construction": true});
            skArc(sketch, "E688.MirrorCS", {"start": v(-118.83, -18.3) * mm, "mid": v(-119.15, -18.44) * mm, "end": v(-119.48, -18.34) * mm});
            skArc(sketch, "E689.MirrorCS", {"start": v(-113.9, -21.18) * mm, "mid": v(-114.17, -20.97) * mm, "end": v(-114.24, -20.63) * mm});
            skLineSegment(sketch, "E690.MirrorCS", {"start": v(-117.88, 16.1) * mm, "end": v(-116.67, 16.97) * mm, "construction": true});
            skArc(sketch, "E691.MirrorCS", {"start": v(-111.9, 24.9) * mm, "mid": v(-112.15, 25.13) * mm, "end": v(-112.5, 25.14) * mm});
            skArc(sketch, "E692.MirrorCS", {"start": v(-97.1, 24.14) * mm, "mid": v(-97.17, 24.48) * mm, "end": v(-97.45, 24.7) * mm});
            skLineSegment(sketch, "E693.MirrorCS", {"start": v(-117.88, 16.1) * mm, "end": v(-115.47, 17.84) * mm});
            skArc(sketch, "E694.MirrorCS", {"start": v(-106.28, 26.15) * mm, "mid": v(-106.61, 26.03) * mm, "end": v(-106.79, 25.73) * mm});
            skLineSegment(sketch, "E695.MirrorCS", {"start": v(-106.28, 26.15) * mm, "end": v(-104.92, 26.14) * mm});
            skLineSegment(sketch, "E696.MirrorCS", {"start": v(-107.11, 20.55) * mm, "end": v(-104.14, 20.54) * mm});
            skLineSegment(sketch, "E697.MirrorCS", {"start": v(-107.11, 20.55) * mm, "end": v(-105.63, 20.55) * mm, "construction": true});
            skArc(sketch, "E698.MirrorCS", {"start": v(-107.61, 21.15) * mm, "mid": v(-107.5, 20.74) * mm, "end": v(-107.11, 20.55) * mm});
            skLineSegment(sketch, "E699.MirrorCS", {"start": v(-101.26, 20.06) * mm, "end": v(-98.43, 19.13) * mm});
            skArc(sketch, "E700.MirrorCS", {"start": v(-120.58, -17.54) * mm, "mid": v(-120.78, -17.25) * mm, "end": v(-120.74, -16.9) * mm});
            skArc(sketch, "E701.MirrorCS", {"start": v(-113.8, 24.72) * mm, "mid": v(-114.07, 24.5) * mm, "end": v(-114.15, 24.17) * mm});
            skLineSegment(sketch, "E702.MirrorCS", {"start": v(-112.85, 19.15) * mm, "end": v(-111.44, 19.6) * mm, "construction": true});
            skArc(sketch, "E703.MirrorCS", {"start": v(-98.74, 25.12) * mm, "mid": v(-99.09, 25.11) * mm, "end": v(-99.35, 24.88) * mm});
            skArc(sketch, "E704.MirrorCS", {"start": v(-120.5, 21.1) * mm, "mid": v(-120.7, 20.82) * mm, "end": v(-120.66, 20.47) * mm});
            skLineSegment(sketch, "E705.MirrorCS", {"start": v(-112.85, 19.15) * mm, "end": v(-110.02, 20.06) * mm});
            skArc(sketch, "E706.MirrorCS", {"start": v(-118.74, 21.86) * mm, "mid": v(-119.06, 22) * mm, "end": v(-119.4, 21.9) * mm});
            skLineSegment(sketch, "E707.MirrorCS", {"start": v(-101.26, 20.06) * mm, "end": v(-99.84, 19.6) * mm, "construction": true});
            skArc(sketch, "E708.MirrorCS", {"start": v(-101.55, 20.79) * mm, "mid": v(-101.57, 20.36) * mm, "end": v(-101.26, 20.06) * mm});
            skLineSegment(sketch, "E709.MirrorCS", {"start": v(-98.74, 25.12) * mm, "end": v(-97.45, 24.7) * mm});
            skArc(sketch, "E710.MirrorCS", {"start": v(-112, -21.36) * mm, "mid": v(-112.25, -21.6) * mm, "end": v(-112.6, -21.6) * mm});
            skArc(sketch, "E711.MirrorCS", {"start": v(-113.51, 19.56) * mm, "mid": v(-113.28, 19.2) * mm, "end": v(-112.85, 19.15) * mm});
            skLineSegment(sketch, "E712.MirrorCS", {"start": v(-120.58, -17.54) * mm, "end": v(-119.48, -18.34) * mm});
            skArc(sketch, "E713.MirrorCS", {"start": v(-104.42, 25.72) * mm, "mid": v(-104.6, 26.02) * mm, "end": v(-104.92, 26.14) * mm});
            skArc(sketch, "E714.MirrorCS", {"start": v(-104.14, 20.54) * mm, "mid": v(-103.75, 20.72) * mm, "end": v(-103.63, 21.14) * mm});
            skLineSegment(sketch, "E715.MirrorCS", {"start": v(-107.72, 20.56) * mm, "end": v(-103.53, 20.54) * mm, "construction": true});
            skArc(sketch, "E716.MirrorCS", {"start": v(-98.43, 19.13) * mm, "mid": v(-98, 19.18) * mm, "end": v(-97.77, 19.54) * mm});
            skLineSegment(sketch, "E717.MirrorCS", {"start": v(-101.83, 20.25) * mm, "end": v(-97.86, 18.94) * mm, "construction": true});
            skLineSegment(sketch, "E718.MirrorCS", {"start": v(-113.8, 24.72) * mm, "end": v(-112.5, 25.14) * mm});
            skLineSegment(sketch, "E719.MirrorCS", {"start": v(-120.5, 21.1) * mm, "end": v(-119.4, 21.9) * mm});
            skLineSegment(sketch, "E720.MirrorCS", {"start": v(-118.37, 15.74) * mm, "end": v(-114.97, 18.2) * mm, "construction": true});
            skLineSegment(sketch, "E721.MirrorCS", {"start": v(-113.43, 18.96) * mm, "end": v(-109.44, 20.25) * mm, "construction": true});
            skLineSegment(sketch, "E722.MirrorCS", {"start": v(-113.9, -21.18) * mm, "end": v(-112.6, -21.6) * mm});
            skArc(sketch, "E723.MirrorCS", {"start": v(-115.47, 17.84) * mm, "mid": v(-115.26, 18.21) * mm, "end": v(-115.4, 18.62) * mm});
            skArc(sketch, "E724.MirrorCS", {"start": v(-110.02, 20.06) * mm, "mid": v(-109.7, 20.35) * mm, "end": v(-109.73, 20.78) * mm});
            skLineSegment(sketch, "E725.MirrorCS", {"start": v(-118.7, -12.73) * mm, "end": v(-120.74, -16.9) * mm});
            skLineSegment(sketch, "E726.MirrorCS", {"start": v(-113.25, -21.4) * mm, "end": v(-111.51, -16.07) * mm});
            skPoint(sketch, "E727.MirrorP", {"position": v(-113.5, -15.43) * mm});
            skLineSegment(sketch, "E728.MirrorCS", {"start": v(-120.03, -17.94) * mm, "end": v(-116.74, -13.42) * mm});
            skPoint(sketch, "E729.MirrorP", {"position": v(-109.52, -16.72) * mm});
            skLineSegment(sketch, "E730.MirrorCS", {"start": v(-118.83, -18.3) * mm, "end": v(-115.48, -15.07) * mm});
            skLineSegment(sketch, "E731.MirrorCS", {"start": v(-113.59, -16.03) * mm, "end": v(-114.24, -20.63) * mm});
            skPoint(sketch, "E732.MirrorP", {"position": v(-115.04, -14.65) * mm});
            skPoint(sketch, "E733.MirrorP", {"position": v(-118.43, -12.18) * mm});
            skLineSegment(sketch, "E734.MirrorCS", {"start": v(-119.95, 21.5) * mm, "end": v(-116.67, 16.97) * mm});
            skPoint(sketch, "E735.MirrorP", {"position": v(-114.3, -21.05) * mm});
            skPoint(sketch, "E736.MirrorP", {"position": v(-119.13, -18.6) * mm});
            skLineSegment(sketch, "E737.MirrorCS", {"start": v(-105.6, 26.14) * mm, "end": v(-105.63, 20.55) * mm});
            skLineSegment(sketch, "E738.MirrorCS", {"start": v(-104.42, 25.72) * mm, "end": v(-103.63, 21.14) * mm});
            skLineSegment(sketch, "E739.MirrorCS", {"start": v(-107.61, 21.15) * mm, "end": v(-106.79, 25.73) * mm});
            skLineSegment(sketch, "E740.MirrorCS", {"start": v(-118.74, 21.86) * mm, "end": v(-115.4, 18.62) * mm});
            skPoint(sketch, "E741.MirrorP", {"position": v(-120.92, -17.29) * mm});
            skPoint(sketch, "E742.MirrorP", {"position": v(-99.14, 25.26) * mm});
            skPoint(sketch, "E743.MirrorP", {"position": v(-113.43, 18.96) * mm});
            skLineSegment(sketch, "E744.MirrorCS", {"start": v(-113.15, 24.93) * mm, "end": v(-111.44, 19.6) * mm});
            skPoint(sketch, "E745.MirrorP", {"position": v(-112.1, 25.27) * mm});
            skPoint(sketch, "E746.MirrorP", {"position": v(-120.84, 20.86) * mm});
            skPoint(sketch, "E747.MirrorP", {"position": v(-97.04, 24.56) * mm});
            skPoint(sketch, "E748.MirrorP", {"position": v(-106.71, 26.15) * mm});
            skLineSegment(sketch, "E749.MirrorCS", {"start": v(-113.51, 19.56) * mm, "end": v(-114.15, 24.17) * mm});
            skPoint(sketch, "E750.MirrorP", {"position": v(-107.8, -17.04) * mm});
            skLineSegment(sketch, "E751.MirrorCS", {"start": v(-97.1, 24.14) * mm, "end": v(-97.77, 19.54) * mm});
            skPoint(sketch, "E752.MirrorP", {"position": v(-103.53, 20.54) * mm});
            skPoint(sketch, "E753.MirrorP", {"position": v(-101.83, 20.25) * mm});
            skPoint(sketch, "E754.MirrorP", {"position": v(-114.97, 18.2) * mm});
            skLineSegment(sketch, "E755.MirrorCS", {"start": v(-101.55, 20.79) * mm, "end": v(-99.35, 24.88) * mm});
            skPoint(sketch, "E756.MirrorP", {"position": v(-118.37, 15.74) * mm});
            skPoint(sketch, "E757.MirrorP", {"position": v(-109.44, 20.25) * mm});
            skPoint(sketch, "E758.MirrorP", {"position": v(-107.72, 20.56) * mm});
            skLineSegment(sketch, "E759.MirrorCS", {"start": v(-111.9, 24.9) * mm, "end": v(-109.73, 20.78) * mm});
            skPoint(sketch, "E760.MirrorP", {"position": v(-97.86, 18.94) * mm});
            skLineSegment(sketch, "E761.MirrorCS", {"start": v(-112, -21.36) * mm, "end": v(-109.8, -17.26) * mm});
            skPoint(sketch, "E762.MirrorP", {"position": v(-119.05, 22.15) * mm});
            skLineSegment(sketch, "E763.MirrorCS", {"start": v(-118.63, 16.29) * mm, "end": v(-120.66, 20.47) * mm});
            skPoint(sketch, "E764.MirrorP", {"position": v(-104.5, 26.14) * mm});
            skPoint(sketch, "E765.MirrorP", {"position": v(-112.2, -21.74) * mm});
            skLineSegment(sketch, "E766.MirrorCS", {"start": v(-107.2, -17.04) * mm, "end": v(-104.22, -17.04) * mm});
            skArc(sketch, "E767.MirrorCS", {"start": v(-106.39, -22.64) * mm, "mid": v(-106.71, -22.52) * mm, "end": v(-106.89, -22.22) * mm});
            skLineSegment(sketch, "E768.MirrorCS", {"start": v(-106.39, -22.64) * mm, "end": v(-105.02, -22.64) * mm});
            skArc(sketch, "E769.MirrorCS", {"start": v(-104.52, -22.22) * mm, "mid": v(-104.7, -22.52) * mm, "end": v(-105.02, -22.64) * mm});
            skArc(sketch, "E770.MirrorCS", {"start": v(-105.05, -22.64) * mm, "mid": v(-104.72, -22.53) * mm, "end": v(-104.55, -22.22) * mm});
            skArc(sketch, "E771.MirrorCS", {"start": v(-106.9, -22.21) * mm, "mid": v(-106.74, -22.52) * mm, "end": v(-106.4, -22.64) * mm});
            skLineSegment(sketch, "E772.MirrorCS", {"start": v(-105.05, -22.64) * mm, "end": v(-106.4, -22.64) * mm});
            skLineSegment(sketch, "E773.MirrorCS", {"start": v(-104.22, -17.05) * mm, "end": v(-107.2, -17.04) * mm});
            skLineSegment(sketch, "E774.MirrorCS", {"start": v(-107.8, -17.04) * mm, "end": v(-103.61, -17.04) * mm, "construction": true});
            skArc(sketch, "E775.MirrorCS", {"start": v(-104.22, -17.04) * mm, "mid": v(-103.83, -17.23) * mm, "end": v(-103.72, -17.64) * mm});
            skArc(sketch, "E776.MirrorCS", {"start": v(-107.7, -17.64) * mm, "mid": v(-107.58, -17.23) * mm, "end": v(-107.2, -17.04) * mm});
            skArc(sketch, "E777.MirrorCS", {"start": v(-107.2, -17.04) * mm, "mid": v(-107.58, -17.22) * mm, "end": v(-107.7, -17.63) * mm});
            skLineSegment(sketch, "E778.MirrorCS", {"start": v(-103.61, -17.05) * mm, "end": v(-107.8, -17.03) * mm, "construction": true});
            skLineSegment(sketch, "E779.MirrorCS", {"start": v(-104.22, -17.05) * mm, "end": v(-105.7, -17.04) * mm, "construction": true});
            skArc(sketch, "E780.MirrorCS", {"start": v(-103.72, -17.65) * mm, "mid": v(-103.83, -17.23) * mm, "end": v(-104.22, -17.05) * mm});
            skLineSegment(sketch, "E781.MirrorCS", {"start": v(-107.2, -17.04) * mm, "end": v(-105.7, -17.04) * mm, "construction": true});
            skPoint(sketch, "E782.MirrorP", {"position": v(-109.5, -16.75) * mm});
            skLineSegment(sketch, "E783.MirrorCS", {"start": v(-104.52, -22.22) * mm, "end": v(-103.72, -17.64) * mm});
            skLineSegment(sketch, "E784.MirrorCS", {"start": v(-105.7, -22.64) * mm, "end": v(-105.7, -17.04) * mm});
            skPoint(sketch, "E785.MirrorP", {"position": v(-104.6, -22.64) * mm});
            skPoint(sketch, "E786.MirrorP", {"position": v(-107.8, -17.03) * mm});
            skPoint(sketch, "E787.MirrorP", {"position": v(-106.81, -22.64) * mm});
            skLineSegment(sketch, "E788.MirrorCS", {"start": v(-105.73, -22.64) * mm, "end": v(-105.7, -17.04) * mm});
            skLineSegment(sketch, "E789.MirrorCS", {"start": v(-106.9, -22.21) * mm, "end": v(-107.7, -17.63) * mm});
            skLineSegment(sketch, "E790.MirrorCS", {"start": v(-103.72, -17.65) * mm, "end": v(-104.55, -22.22) * mm});
            skLineSegment(sketch, "E791.MirrorCS", {"start": v(-107.7, -17.64) * mm, "end": v(-106.89, -22.22) * mm});
            skPoint(sketch, "E792.MirrorP", {"position": v(-106.84, -22.64) * mm});
            skPoint(sketch, "E793.MirrorP", {"position": v(-104.62, -22.64) * mm});
            skPoint(sketch, "E794.MirrorP", {"position": v(-101.91, -16.76) * mm});
            skPoint(sketch, "E795.MirrorP", {"position": v(-103.61, -17.04) * mm});
            skArc(sketch, "E796.MirrorCS", {"start": v(-86.27, -0.27) * mm, "mid": v(-86.69, -0.16) * mm, "end": v(-86.87, 0.23) * mm});
            skLineSegment(sketch, "E797.MirrorCS", {"start": v(-86.87, 0.23) * mm, "end": v(-86.87, 1.72) * mm, "construction": true});
            skLineSegment(sketch, "E798.MirrorCS", {"start": v(-86.87, 0.23) * mm, "end": v(-86.87, 3.2) * mm});
            skLineSegment(sketch, "E799.MirrorCS", {"start": v(-86.87, -0.38) * mm, "end": v(-86.87, 3.81) * mm, "construction": true});
            skArc(sketch, "E800.MirrorCS", {"start": v(-86.87, 3.2) * mm, "mid": v(-86.69, 3.6) * mm, "end": v(-86.27, 3.7) * mm});
            skLineSegment(sketch, "E801.MirrorCS", {"start": v(-81.27, 1.04) * mm, "end": v(-81.27, 2.4) * mm});
            skArc(sketch, "E802.MirrorCS", {"start": v(-81.7, 2.9) * mm, "mid": v(-81.4, 2.72) * mm, "end": v(-81.27, 2.4) * mm});
            skArc(sketch, "E803.MirrorCS", {"start": v(-81.27, 1.04) * mm, "mid": v(-81.4, 0.7) * mm, "end": v(-81.7, 0.53) * mm});
            skLineSegment(sketch, "E804.MirrorCS", {"start": v(-86.27, -0.27) * mm, "end": v(-81.7, 0.53) * mm});
            skLineSegment(sketch, "E805.MirrorCS", {"start": v(-81.7, 2.9) * mm, "end": v(-86.27, 3.7) * mm});
            skPoint(sketch, "E806.MirrorP", {"position": v(-86.87, 3.81) * mm});
            skLineSegment(sketch, "E807.MirrorCS", {"start": v(-81.27, 1.72) * mm, "end": v(-86.87, 1.72) * mm});
            skPoint(sketch, "E808.MirrorP", {"position": v(-86.87, -0.38) * mm});
            skPoint(sketch, "E809.MirrorP", {"position": v(-81.27, 0.6) * mm});
            skPoint(sketch, "E810.MirrorP", {"position": v(-81.27, 2.82) * mm});
            skArc(sketch, "E811.MirrorCS", {"start": v(-86.61, 5.8) * mm, "mid": v(-87.04, 5.77) * mm, "end": v(-87.34, 6.09) * mm});
            skLineSegment(sketch, "E812.MirrorCS", {"start": v(-87.34, 6.09) * mm, "end": v(-87.8, 7.5) * mm, "construction": true});
            skLineSegment(sketch, "E813.MirrorCS", {"start": v(-87.34, 6.09) * mm, "end": v(-88.26, 8.92) * mm});
            skLineSegment(sketch, "E814.MirrorCS", {"start": v(-87.15, 5.51) * mm, "end": v(-88.44, 9.5) * mm, "construction": true});
            skArc(sketch, "E815.MirrorCS", {"start": v(-88.26, 8.92) * mm, "mid": v(-88.2, 9.34) * mm, "end": v(-87.84, 9.58) * mm});
            skLineSegment(sketch, "E816.MirrorCS", {"start": v(-82.26, 8.58) * mm, "end": v(-82.68, 9.88) * mm});
            skArc(sketch, "E817.MirrorCS", {"start": v(-83.24, 10.23) * mm, "mid": v(-82.9, 10.15) * mm, "end": v(-82.68, 9.88) * mm});
            skArc(sketch, "E818.MirrorCS", {"start": v(-82.26, 8.58) * mm, "mid": v(-82.28, 8.24) * mm, "end": v(-82.5, 7.98) * mm});
            skLineSegment(sketch, "E819.MirrorCS", {"start": v(-86.61, 5.8) * mm, "end": v(-82.5, 7.98) * mm});
            skLineSegment(sketch, "E820.MirrorCS", {"start": v(-83.24, 10.23) * mm, "end": v(-87.84, 9.58) * mm});
            skPoint(sketch, "E821.MirrorP", {"position": v(-88.44, 9.5) * mm});
            skLineSegment(sketch, "E822.MirrorCS", {"start": v(-82.47, 9.23) * mm, "end": v(-87.8, 7.5) * mm});
            skPoint(sketch, "E823.MirrorP", {"position": v(-87.15, 5.51) * mm});
            skPoint(sketch, "E824.MirrorP", {"position": v(-82.13, 8.18) * mm});
            skPoint(sketch, "E825.MirrorP", {"position": v(-82.82, 10.29) * mm});
            skArc(sketch, "E826.MirrorCS", {"start": v(-91.18, -11.27) * mm, "mid": v(-91.45, -10.94) * mm, "end": v(-91.37, -10.52) * mm});
            skLineSegment(sketch, "E827.MirrorCS", {"start": v(-91.37, -10.52) * mm, "end": v(-90.5, -9.31) * mm, "construction": true});
            skLineSegment(sketch, "E828.MirrorCS", {"start": v(-91.37, -10.52) * mm, "end": v(-89.62, -8.11) * mm});
            skLineSegment(sketch, "E829.MirrorCS", {"start": v(-91.73, -11) * mm, "end": v(-89.26, -7.62) * mm, "construction": true});
            skArc(sketch, "E830.MirrorCS", {"start": v(-89.62, -8.11) * mm, "mid": v(-89.24, -7.9) * mm, "end": v(-88.84, -8.06) * mm});
            skLineSegment(sketch, "E831.MirrorCS", {"start": v(-86.37, -13.16) * mm, "end": v(-85.57, -12.06) * mm});
            skArc(sketch, "E832.MirrorCS", {"start": v(-85.62, -11.4) * mm, "mid": v(-85.48, -11.72) * mm, "end": v(-85.57, -12.06) * mm});
            skArc(sketch, "E833.MirrorCS", {"start": v(-86.37, -13.16) * mm, "mid": v(-86.66, -13.35) * mm, "end": v(-87, -13.32) * mm});
            skLineSegment(sketch, "E834.MirrorCS", {"start": v(-91.18, -11.27) * mm, "end": v(-87, -13.32) * mm});
            skLineSegment(sketch, "E835.MirrorCS", {"start": v(-85.62, -11.4) * mm, "end": v(-88.84, -8.06) * mm});
            skPoint(sketch, "E836.MirrorP", {"position": v(-89.26, -7.62) * mm});
            skLineSegment(sketch, "E837.MirrorCS", {"start": v(-85.97, -12.6) * mm, "end": v(-90.5, -9.31) * mm});
            skPoint(sketch, "E838.MirrorP", {"position": v(-91.73, -11) * mm});
            skPoint(sketch, "E839.MirrorP", {"position": v(-86.62, -13.5) * mm});
            skPoint(sketch, "E840.MirrorP", {"position": v(-85.32, -11.71) * mm});
            skArc(sketch, "E841.MirrorCS", {"start": v(-87.89, -6.17) * mm, "mid": v(-88.25, -5.93) * mm, "end": v(-88.3, -5.5) * mm});
            skLineSegment(sketch, "E842.MirrorCS", {"start": v(-88.3, -5.5) * mm, "end": v(-87.84, -4.09) * mm, "construction": true});
            skLineSegment(sketch, "E843.MirrorCS", {"start": v(-88.3, -5.5) * mm, "end": v(-87.38, -2.67) * mm});
            skLineSegment(sketch, "E844.MirrorCS", {"start": v(-88.49, -6.08) * mm, "end": v(-87.19, -2.1) * mm, "construction": true});
            skArc(sketch, "E845.MirrorCS", {"start": v(-87.38, -2.67) * mm, "mid": v(-87.08, -2.36) * mm, "end": v(-86.65, -2.38) * mm});
            skLineSegment(sketch, "E846.MirrorCS", {"start": v(-82.73, -6.47) * mm, "end": v(-82.3, -5.18) * mm});
            skArc(sketch, "E847.MirrorCS", {"start": v(-82.55, -4.57) * mm, "mid": v(-82.32, -4.83) * mm, "end": v(-82.3, -5.18) * mm});
            skArc(sketch, "E848.MirrorCS", {"start": v(-82.73, -6.47) * mm, "mid": v(-82.94, -6.75) * mm, "end": v(-83.28, -6.82) * mm});
            skLineSegment(sketch, "E849.MirrorCS", {"start": v(-87.89, -6.17) * mm, "end": v(-83.28, -6.82) * mm});
            skLineSegment(sketch, "E850.MirrorCS", {"start": v(-82.55, -4.57) * mm, "end": v(-86.65, -2.38) * mm});
            skPoint(sketch, "E851.MirrorP", {"position": v(-87.19, -2.1) * mm});
            skLineSegment(sketch, "E852.MirrorCS", {"start": v(-82.52, -5.83) * mm, "end": v(-87.84, -4.09) * mm});
            skPoint(sketch, "E853.MirrorP", {"position": v(-88.49, -6.08) * mm});
            skPoint(sketch, "E854.MirrorP", {"position": v(-82.86, -6.88) * mm});
            skPoint(sketch, "E855.MirrorP", {"position": v(-82.17, -4.77) * mm});
            skArc(sketch, "E856.MirrorCS", {"start": v(-128.64, -6.38) * mm, "mid": v(-128.42, -6.65) * mm, "end": v(-128.08, -6.72) * mm});
            skLineSegment(sketch, "E857.MirrorCS", {"start": v(-120, -10.46) * mm, "end": v(-121.75, -8.04) * mm});
            skLineSegment(sketch, "E858.MirrorCS", {"start": v(-120, -10.46) * mm, "end": v(-120.88, -9.25) * mm, "construction": true});
            skLineSegment(sketch, "E859.MirrorCS", {"start": v(-123.06, -5.43) * mm, "end": v(-123.97, -2.6) * mm});
            skArc(sketch, "E860.MirrorCS", {"start": v(-121.75, -8.04) * mm, "mid": v(-122.13, -7.83) * mm, "end": v(-122.53, -7.99) * mm});
            skArc(sketch, "E861.MirrorCS", {"start": v(-120.2, -11.21) * mm, "mid": v(-119.93, -10.88) * mm, "end": v(-120, -10.46) * mm});
            skLineSegment(sketch, "E862.MirrorCS", {"start": v(-128.64, -6.38) * mm, "end": v(-129.05, -5.08) * mm});
            skLineSegment(sketch, "E863.MirrorCS", {"start": v(-119.65, -10.95) * mm, "end": v(-122.1, -7.55) * mm, "construction": true});
            skArc(sketch, "E864.MirrorCS", {"start": v(-123.48, -6.1) * mm, "mid": v(-123.11, -5.86) * mm, "end": v(-123.06, -5.43) * mm});
            skArc(sketch, "E865.MirrorCS", {"start": v(-125.77, -11.32) * mm, "mid": v(-125.91, -11.64) * mm, "end": v(-125.82, -11.97) * mm});
            skArc(sketch, "E866.MirrorCS", {"start": v(-123.97, -2.6) * mm, "mid": v(-124.26, -2.28) * mm, "end": v(-124.7, -2.3) * mm});
            skArc(sketch, "E867.MirrorCS", {"start": v(-125.02, -13.08) * mm, "mid": v(-124.73, -13.27) * mm, "end": v(-124.38, -13.24) * mm});
            skArc(sketch, "E868.MirrorCS", {"start": v(-128.8, -4.47) * mm, "mid": v(-129.04, -4.73) * mm, "end": v(-129.05, -5.08) * mm});
            skLineSegment(sketch, "E869.MirrorCS", {"start": v(-125.02, -13.08) * mm, "end": v(-125.82, -11.97) * mm});
            skLineSegment(sketch, "E870.MirrorCS", {"start": v(-122.87, -6) * mm, "end": v(-124.16, -2.02) * mm, "construction": true});
            skPoint(sketch, "E871.MirrorP", {"position": v(-124.16, -2.02) * mm});
            skLineSegment(sketch, "E872.MirrorCS", {"start": v(-128.8, -4.47) * mm, "end": v(-124.7, -2.3) * mm});
            skLineSegment(sketch, "E873.MirrorCS", {"start": v(-123.48, -6.1) * mm, "end": v(-128.08, -6.72) * mm});
            skPoint(sketch, "E874.MirrorP", {"position": v(-128.5, -6.78) * mm});
            skPoint(sketch, "E875.MirrorP", {"position": v(-126.07, -11.63) * mm});
            skLineSegment(sketch, "E876.MirrorCS", {"start": v(-123.06, -5.43) * mm, "end": v(-123.52, -4.01) * mm, "construction": true});
            skLineSegment(sketch, "E877.MirrorCS", {"start": v(-125.77, -11.32) * mm, "end": v(-122.53, -7.99) * mm});
            skPoint(sketch, "E878.MirrorP", {"position": v(-122.87, -6) * mm});
            skPoint(sketch, "E879.MirrorP", {"position": v(-119.65, -10.95) * mm});
            skPoint(sketch, "E880.MirrorP", {"position": v(-122.1, -7.55) * mm});
            skPoint(sketch, "E881.MirrorP", {"position": v(-124.77, -13.42) * mm});
            skLineSegment(sketch, "E882.MirrorCS", {"start": v(-120.2, -11.21) * mm, "end": v(-124.38, -13.24) * mm});
            skPoint(sketch, "E883.MirrorP", {"position": v(-124.47, -0.3) * mm});
            skLineSegment(sketch, "E884.MirrorCS", {"start": v(-128.84, -5.73) * mm, "end": v(-123.52, -4.01) * mm});
            skLineSegment(sketch, "E885.MirrorCS", {"start": v(-125.42, -12.53) * mm, "end": v(-120.88, -9.25) * mm});
            skPoint(sketch, "E886.MirrorP", {"position": v(-129.18, -4.67) * mm});
            skArc(sketch, "E887.MirrorCS", {"start": v(-123.44, 9.68) * mm, "mid": v(-123.08, 9.44) * mm, "end": v(-123.03, 9.02) * mm});
            skLineSegment(sketch, "E888.MirrorCS", {"start": v(-123.03, 9.02) * mm, "end": v(-123.95, 6.19) * mm});
            skLineSegment(sketch, "E889.MirrorCS", {"start": v(-119.96, 14.03) * mm, "end": v(-120.83, 12.83) * mm, "construction": true});
            skLineSegment(sketch, "E890.MirrorCS", {"start": v(-123.03, 9.02) * mm, "end": v(-123.5, 7.6) * mm, "construction": true});
            skArc(sketch, "E891.MirrorCS", {"start": v(-121.7, 11.62) * mm, "mid": v(-122.09, 11.42) * mm, "end": v(-122.49, 11.57) * mm});
            skLineSegment(sketch, "E892.MirrorCS", {"start": v(-119.6, 14.52) * mm, "end": v(-122.07, 11.13) * mm, "construction": true});
            skArc(sketch, "E893.MirrorCS", {"start": v(-120.14, 14.79) * mm, "mid": v(-119.87, 14.45) * mm, "end": v(-119.96, 14.03) * mm});
            skLineSegment(sketch, "E894.MirrorCS", {"start": v(-119.96, 14.03) * mm, "end": v(-121.7, 11.62) * mm});
            skArc(sketch, "E895.MirrorCS", {"start": v(-91.13, 14.72) * mm, "mid": v(-91.4, 14.4) * mm, "end": v(-91.32, 13.97) * mm});
            skArc(sketch, "E896.MirrorCS", {"start": v(-123.95, 6.19) * mm, "mid": v(-124.25, 5.87) * mm, "end": v(-124.68, 5.9) * mm});
            skLineSegment(sketch, "E897.MirrorCS", {"start": v(-122.84, 9.6) * mm, "end": v(-124.14, 5.61) * mm, "construction": true});
            skArc(sketch, "E898.MirrorCS", {"start": v(-125.71, 14.92) * mm, "mid": v(-125.85, 15.24) * mm, "end": v(-125.76, 15.57) * mm});
            skArc(sketch, "E899.MirrorCS", {"start": v(-128.6, 9.99) * mm, "mid": v(-128.39, 10.26) * mm, "end": v(-128.05, 10.33) * mm});
            skLineSegment(sketch, "E900.MirrorCS", {"start": v(-91.32, 13.97) * mm, "end": v(-90.45, 12.76) * mm, "construction": true});
            skArc(sketch, "E901.MirrorCS", {"start": v(-82.52, 7.99) * mm, "mid": v(-82.3, 8.24) * mm, "end": v(-82.28, 8.6) * mm});
            skArc(sketch, "E902.MirrorCS", {"start": v(-83.27, -6.8) * mm, "mid": v(-82.93, -6.74) * mm, "end": v(-82.72, -6.46) * mm});
            skLineSegment(sketch, "E903.MirrorCS", {"start": v(-91.32, 13.97) * mm, "end": v(-89.58, 11.56) * mm});
            skArc(sketch, "E904.MirrorCS", {"start": v(-81.27, 2.37) * mm, "mid": v(-81.39, 2.7) * mm, "end": v(-81.69, 2.88) * mm});
            skLineSegment(sketch, "E905.MirrorCS", {"start": v(-81.27, 2.37) * mm, "end": v(-81.28, 1.01) * mm});
            skLineSegment(sketch, "E906.MirrorCS", {"start": v(-86.86, 3.2) * mm, "end": v(-86.87, 0.23) * mm});
            skLineSegment(sketch, "E907.MirrorCS", {"start": v(-86.86, 3.2) * mm, "end": v(-86.87, 1.72) * mm, "construction": true});
            skArc(sketch, "E908.MirrorCS", {"start": v(-86.26, 3.7) * mm, "mid": v(-86.68, 3.6) * mm, "end": v(-86.86, 3.2) * mm});
            skLineSegment(sketch, "E909.MirrorCS", {"start": v(-87.35, -2.65) * mm, "end": v(-88.29, -5.48) * mm});
            skArc(sketch, "E910.MirrorCS", {"start": v(-124.96, 16.67) * mm, "mid": v(-124.67, 16.87) * mm, "end": v(-124.32, 16.83) * mm});
            skArc(sketch, "E911.MirrorCS", {"start": v(-82.7, 9.89) * mm, "mid": v(-82.9, 10.16) * mm, "end": v(-83.25, 10.24) * mm});
            skLineSegment(sketch, "E912.MirrorCS", {"start": v(-88.27, 8.94) * mm, "end": v(-87.81, 7.53) * mm, "construction": true});
            skArc(sketch, "E913.MirrorCS", {"start": v(-82.3, -5.17) * mm, "mid": v(-82.3, -4.82) * mm, "end": v(-82.53, -4.56) * mm});
            skArc(sketch, "E914.MirrorCS", {"start": v(-86.31, 16.6) * mm, "mid": v(-86.6, 16.79) * mm, "end": v(-86.94, 16.75) * mm});
            skLineSegment(sketch, "E915.MirrorCS", {"start": v(-88.27, 8.94) * mm, "end": v(-87.36, 6.11) * mm});
            skArc(sketch, "E916.MirrorCS", {"start": v(-85.56, 14.83) * mm, "mid": v(-85.42, 15.15) * mm, "end": v(-85.51, 15.49) * mm});
            skLineSegment(sketch, "E917.MirrorCS", {"start": v(-87.35, -2.65) * mm, "end": v(-87.82, -4.07) * mm, "construction": true});
            skArc(sketch, "E918.MirrorCS", {"start": v(-86.63, -2.36) * mm, "mid": v(-87.06, -2.34) * mm, "end": v(-87.35, -2.65) * mm});
            skLineSegment(sketch, "E919.MirrorCS", {"start": v(-82.3, -5.17) * mm, "end": v(-82.72, -6.46) * mm});
            skArc(sketch, "E920.MirrorCS", {"start": v(-128.78, 8.08) * mm, "mid": v(-129.01, 8.34) * mm, "end": v(-129.02, 8.7) * mm});
            skArc(sketch, "E921.MirrorCS", {"start": v(-87.85, 9.6) * mm, "mid": v(-88.21, 9.37) * mm, "end": v(-88.27, 8.94) * mm});
            skLineSegment(sketch, "E922.MirrorCS", {"start": v(-124.96, 16.67) * mm, "end": v(-125.76, 15.57) * mm});
            skArc(sketch, "E923.MirrorCS", {"start": v(-81.7, 0.51) * mm, "mid": v(-81.4, 0.69) * mm, "end": v(-81.28, 1.01) * mm});
            skArc(sketch, "E924.MirrorCS", {"start": v(-86.87, 0.23) * mm, "mid": v(-86.7, -0.16) * mm, "end": v(-86.28, -0.27) * mm});
            skLineSegment(sketch, "E925.MirrorCS", {"start": v(-86.86, 3.81) * mm, "end": v(-86.88, -0.38) * mm, "construction": true});
            skArc(sketch, "E926.MirrorCS", {"start": v(-88.29, -5.48) * mm, "mid": v(-88.24, -5.9) * mm, "end": v(-87.88, -6.14) * mm});
            skLineSegment(sketch, "E927.MirrorCS", {"start": v(-87.16, -2.08) * mm, "end": v(-88.48, -6.05) * mm, "construction": true});
            skLineSegment(sketch, "E928.MirrorCS", {"start": v(-82.7, 9.89) * mm, "end": v(-82.28, 8.6) * mm});
            skLineSegment(sketch, "E929.MirrorCS", {"start": v(-86.31, 16.6) * mm, "end": v(-85.51, 15.49) * mm});
            skLineSegment(sketch, "E930.MirrorCS", {"start": v(-91.67, 14.46) * mm, "end": v(-89.22, 11.06) * mm, "construction": true});
            skLineSegment(sketch, "E931.MirrorCS", {"start": v(-88.45, 9.52) * mm, "end": v(-87.17, 5.53) * mm, "construction": true});
            skLineSegment(sketch, "E932.MirrorCS", {"start": v(-128.6, 9.99) * mm, "end": v(-129.02, 8.7) * mm});
            skArc(sketch, "E933.MirrorCS", {"start": v(-89.58, 11.56) * mm, "mid": v(-89.2, 11.35) * mm, "end": v(-88.8, 11.5) * mm});
            skArc(sketch, "E934.MirrorCS", {"start": v(-87.36, 6.11) * mm, "mid": v(-87.06, 5.8) * mm, "end": v(-86.64, 5.82) * mm});
            skLineSegment(sketch, "E935.MirrorCS", {"start": v(-120.14, 14.79) * mm, "end": v(-124.32, 16.83) * mm});
            skLineSegment(sketch, "E936.MirrorCS", {"start": v(-128.81, 9.34) * mm, "end": v(-123.5, 7.6) * mm});
            skPoint(sketch, "E937.MirrorP", {"position": v(-122.84, 9.6) * mm});
            skLineSegment(sketch, "E938.MirrorCS", {"start": v(-125.36, 16.12) * mm, "end": v(-120.83, 12.83) * mm});
            skPoint(sketch, "E939.MirrorP", {"position": v(-124.14, 5.61) * mm});
            skLineSegment(sketch, "E940.MirrorCS", {"start": v(-125.71, 14.92) * mm, "end": v(-122.49, 11.57) * mm});
            skLineSegment(sketch, "E941.MirrorCS", {"start": v(-123.44, 9.68) * mm, "end": v(-128.05, 10.33) * mm});
            skPoint(sketch, "E942.MirrorP", {"position": v(-122.07, 11.13) * mm});
            skPoint(sketch, "E943.MirrorP", {"position": v(-119.6, 14.52) * mm});
            skLineSegment(sketch, "E944.MirrorCS", {"start": v(-85.91, 16.04) * mm, "end": v(-90.45, 12.76) * mm});
            skPoint(sketch, "E945.MirrorP", {"position": v(-128.47, 10.4) * mm});
            skPoint(sketch, "E946.MirrorP", {"position": v(-126, 15.22) * mm});
            skLineSegment(sketch, "E947.MirrorCS", {"start": v(-81.7, 0.51) * mm, "end": v(-86.28, -0.27) * mm});
            skLineSegment(sketch, "E948.MirrorCS", {"start": v(-86.26, 3.7) * mm, "end": v(-81.69, 2.88) * mm});
            skLineSegment(sketch, "E949.MirrorCS", {"start": v(-85.56, 14.83) * mm, "end": v(-88.8, 11.5) * mm});
            skPoint(sketch, "E950.MirrorP", {"position": v(-82.82, 10.3) * mm});
            skPoint(sketch, "E951.MirrorP", {"position": v(-124.7, 17.02) * mm});
            skPoint(sketch, "E952.MirrorP", {"position": v(-82.16, -4.77) * mm});
            skPoint(sketch, "E953.MirrorP", {"position": v(-88.45, 9.52) * mm});
            skPoint(sketch, "E954.MirrorP", {"position": v(-82.15, 8.19) * mm});
            skPoint(sketch, "E955.MirrorP", {"position": v(-86.56, 16.93) * mm});
            skPoint(sketch, "E956.MirrorP", {"position": v(-82.85, -6.87) * mm});
            skPoint(sketch, "E957.MirrorP", {"position": v(-81.27, 2.8) * mm});
            skLineSegment(sketch, "E958.MirrorCS", {"start": v(-87.85, 9.6) * mm, "end": v(-83.25, 10.24) * mm});
            skPoint(sketch, "E959.MirrorP", {"position": v(-124.46, 3.9) * mm});
            skLineSegment(sketch, "E960.MirrorCS", {"start": v(-83.27, -6.8) * mm, "end": v(-87.88, -6.14) * mm});
            skPoint(sketch, "E961.MirrorP", {"position": v(-86.88, -0.38) * mm});
            skPoint(sketch, "E962.MirrorP", {"position": v(-87.16, -2.08) * mm});
            skPoint(sketch, "E963.MirrorP", {"position": v(-89.22, 11.06) * mm});
            skLineSegment(sketch, "E964.MirrorCS", {"start": v(-86.63, -2.36) * mm, "end": v(-82.53, -4.56) * mm});
            skPoint(sketch, "E965.MirrorP", {"position": v(-91.67, 14.46) * mm});
            skPoint(sketch, "E966.MirrorP", {"position": v(-87.17, 5.53) * mm});
            skPoint(sketch, "E967.MirrorP", {"position": v(-86.86, 3.81) * mm});
            skLineSegment(sketch, "E968.MirrorCS", {"start": v(-82.52, 7.99) * mm, "end": v(-86.64, 5.82) * mm});
            skPoint(sketch, "E969.MirrorP", {"position": v(-88.48, -6.05) * mm});
            skLineSegment(sketch, "E970.MirrorCS", {"start": v(-128.78, 8.08) * mm, "end": v(-124.68, 5.9) * mm});
            skPoint(sketch, "E971.MirrorP", {"position": v(-85.26, 15.14) * mm});
            skLineSegment(sketch, "E972.MirrorCS", {"start": v(-91.13, 14.72) * mm, "end": v(-86.94, 16.75) * mm});
            skPoint(sketch, "E973.MirrorP", {"position": v(-81.28, 0.59) * mm});
            skPoint(sketch, "E974.MirrorP", {"position": v(-129.16, 8.29) * mm});
            skLineSegment(sketch, "E975.MirrorCS", {"start": v(-124.46, 3.28) * mm, "end": v(-124.46, 0.3) * mm});
            skArc(sketch, "E976.MirrorCS", {"start": v(-130.06, 2.48) * mm, "mid": v(-129.94, 2.8) * mm, "end": v(-129.64, 2.98) * mm});
            skLineSegment(sketch, "E977.MirrorCS", {"start": v(-130.06, 2.48) * mm, "end": v(-130.06, 1.12) * mm});
            skArc(sketch, "E978.MirrorCS", {"start": v(-129.64, 0.61) * mm, "mid": v(-129.94, 0.79) * mm, "end": v(-130.06, 1.12) * mm});
            skArc(sketch, "E979.MirrorCS", {"start": v(-130.06, 1.14) * mm, "mid": v(-129.94, 0.81) * mm, "end": v(-129.64, 0.64) * mm});
            skArc(sketch, "E980.MirrorCS", {"start": v(-129.63, 3) * mm, "mid": v(-129.93, 2.83) * mm, "end": v(-130.05, 2.5) * mm});
            skLineSegment(sketch, "E981.MirrorCS", {"start": v(-130.06, 1.14) * mm, "end": v(-130.05, 2.5) * mm});
            skLineSegment(sketch, "E982.MirrorCS", {"start": v(-124.47, 0.3) * mm, "end": v(-124.45, 3.28) * mm});
            skLineSegment(sketch, "E983.MirrorCS", {"start": v(-124.46, 3.9) * mm, "end": v(-124.46, -0.3) * mm, "construction": true});
            skArc(sketch, "E984.MirrorCS", {"start": v(-124.46, 0.3) * mm, "mid": v(-124.64, -0.08) * mm, "end": v(-125.06, -0.2) * mm});
            skArc(sketch, "E985.MirrorCS", {"start": v(-125.06, 3.79) * mm, "mid": v(-124.64, 3.67) * mm, "end": v(-124.46, 3.28) * mm});
            skArc(sketch, "E986.MirrorCS", {"start": v(-124.45, 3.28) * mm, "mid": v(-124.63, 3.67) * mm, "end": v(-125.05, 3.79) * mm});
            skLineSegment(sketch, "E987.MirrorCS", {"start": v(-124.47, -0.3) * mm, "end": v(-124.45, 3.9) * mm, "construction": true});
            skLineSegment(sketch, "E988.MirrorCS", {"start": v(-124.47, 0.3) * mm, "end": v(-124.46, 1.8) * mm, "construction": true});
            skArc(sketch, "E989.MirrorCS", {"start": v(-125.07, -0.2) * mm, "mid": v(-124.65, -0.08) * mm, "end": v(-124.47, 0.3) * mm});
            skLineSegment(sketch, "E990.MirrorCS", {"start": v(-124.46, 3.28) * mm, "end": v(-124.46, 1.8) * mm, "construction": true});
            skPoint(sketch, "E991.MirrorP", {"position": v(-124.16, 5.59) * mm});
            skLineSegment(sketch, "E992.MirrorCS", {"start": v(-129.64, 0.61) * mm, "end": v(-125.06, -0.2) * mm});
            skLineSegment(sketch, "E993.MirrorCS", {"start": v(-130.06, 1.8) * mm, "end": v(-124.46, 1.8) * mm});
            skPoint(sketch, "E994.MirrorP", {"position": v(-130.06, 0.69) * mm});
            skPoint(sketch, "E995.MirrorP", {"position": v(-124.45, 3.9) * mm});
            skPoint(sketch, "E996.MirrorP", {"position": v(-130.06, 2.9) * mm});
            skLineSegment(sketch, "E997.MirrorCS", {"start": v(-130.06, 1.82) * mm, "end": v(-124.46, 1.8) * mm});
            skLineSegment(sketch, "E998.MirrorCS", {"start": v(-129.63, 3) * mm, "end": v(-125.05, 3.79) * mm});
            skLineSegment(sketch, "E999.MirrorCS", {"start": v(-125.07, -0.2) * mm, "end": v(-129.64, 0.64) * mm});
            skLineSegment(sketch, "E1000.MirrorCS", {"start": v(-125.06, 3.79) * mm, "end": v(-129.64, 2.98) * mm});
            skPoint(sketch, "E1001.MirrorP", {"position": v(-130.05, 2.93) * mm});
            skPoint(sketch, "E1002.MirrorP", {"position": v(-130.06, 0.71) * mm});
            skPoint(sketch, "E1003.MirrorP", {"position": v(-124.18, -2) * mm});
            skPoint(sketch, "E1004.MirrorP", {"position": v(-124.46, -0.3) * mm});
            skSolve(sketch);
        }
        {
            var Q0;
            Q0 = qSketchRegion(id + "F4", true);
            extrude(context, id + "F5", {"entities" : qUnion([Q0]), "operationType" : NewBodyOperationType.ADD, "depth" : 6.35 * mm});
        }
        {
            var Q0;
            Q0 = qSketchRegion(id + "F3", true);
            extrude(context, id + "F6", {"entities" : qUnion([Q0]), "operationType" : NewBodyOperationType.ADD, "depth" : 12.7 * mm, "offsetDistance" : 25.4 * mm});
        }
    });
